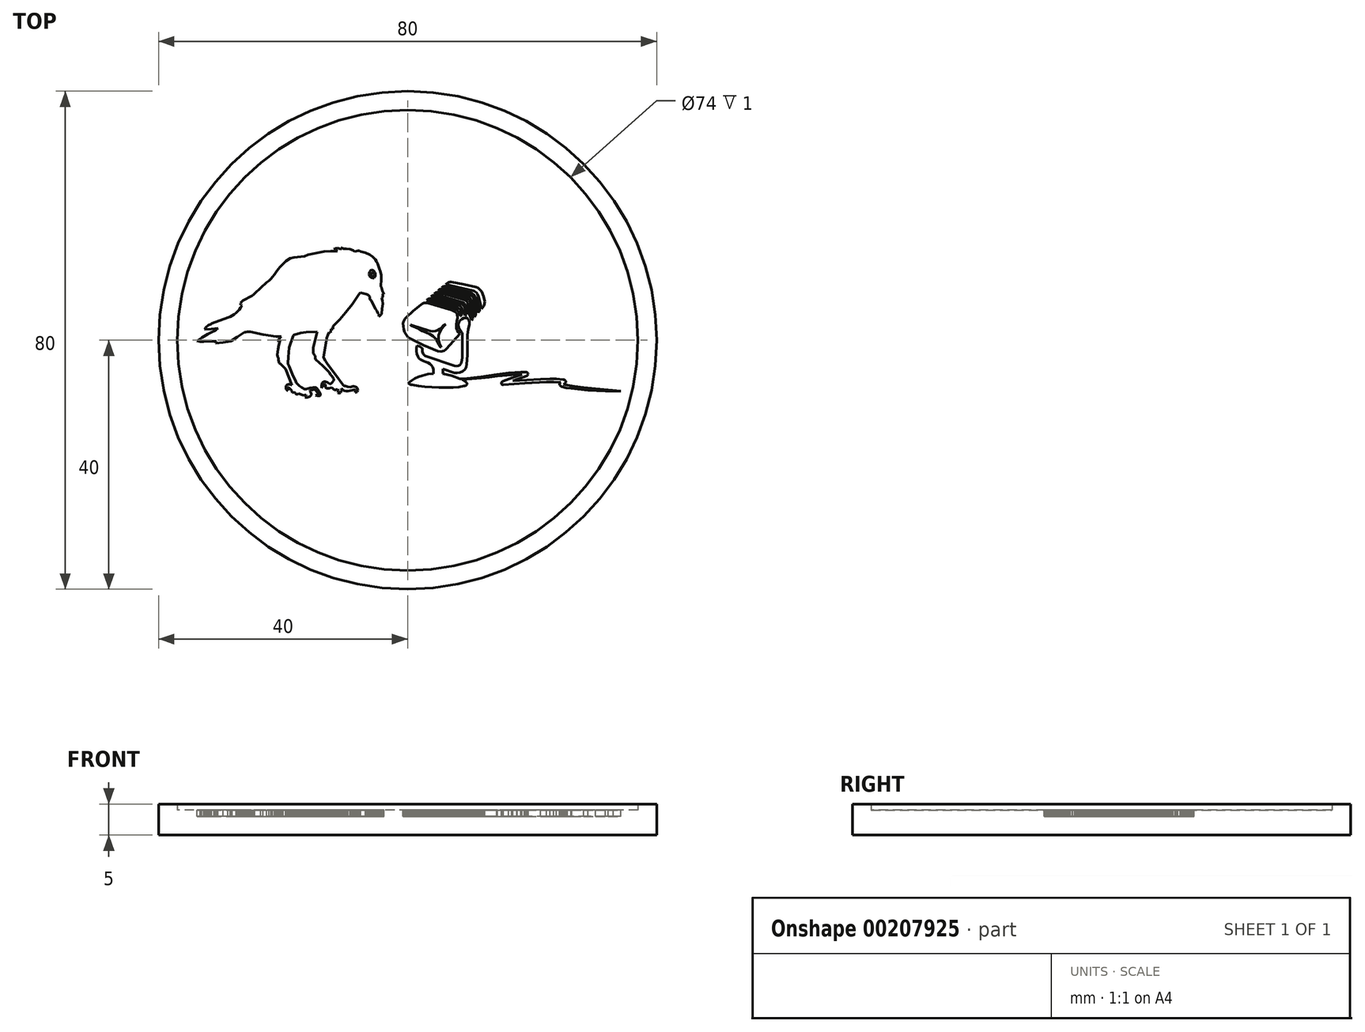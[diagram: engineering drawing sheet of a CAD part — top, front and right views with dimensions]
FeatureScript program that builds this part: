
annotation { "Feature Type Name" : "Feature", "Feature Type Description" : "" }
export const myFeature = defineFeature(function(context is Context, id is Id, definition is map)
    precondition{}
    {
        {
            var Q0;
            Q0=qCreatedBy(makeId("Top.planeOp"),FACE);
            var sketch = newSketch(context, id + "F0", { "sketchPlane" : qUnion([Q0])});
            skCircle(sketch, "E0", {"center": v(0, 0) * mm, "radius": 40 * mm});
            skSolve(sketch);
        }
        {
            var Q0;
            Q0 = qSketchRegion(id + "F0", true);
            extrude(context, id + "F1", {"entities" : qUnion([Q0]), "depth" : 4 * mm});
        }
        {
            var Q0;
            Q0=makeQuery(id+"F1.opExtrude","CAP_FACE",FACE,{"disambiguationData":[OSD([sQuery(id+"F0.wireOp",EDGE,"E0")])],"isStart":false});
            var sketch = newSketch(context, id + "F2", { "sketchPlane" : qUnion([Q0])});
            skCircle(sketch, "E1", {"center": v(0, 0) * mm, "radius": 37 * mm});
            skSolve(sketch);
        }
        {
            var Q0;
            Q0=makeQuery(id+"F2.imprint","IMPRINT",FACE,{"disambiguationData":[TD([[makeQuery(id+"F2.imprint","IMPRINT",EDGE,{"derivedFrom":sQuery(id+"F2.wireOp",EDGE,"E1")}),-1.0]])]});
            extrude(context, id + "F3", {"entities" : qUnion([Q0]), "operationType" : NewBodyOperationType.ADD, "depth" : 1 * mm});
        }
        {
            var Q0;
            Q0=makeQuery(id+"F3.opExtrude","CAP_FACE",FACE,{"disambiguationData":[OSD([sQuery(id+"F0.wireOp",EDGE,"E0"),sQuery(id+"F2.wireOp",EDGE,"E1")])],"isStart":false});
            var sketch = newSketch(context, id + "F4", { "sketchPlane" : qUnion([Q0])});
            skLineSegment(sketch, "E2", {"start": v(-11.88, 14.64) * mm, "end": v(-11.55, 14.76) * mm});
            skLineSegment(sketch, "E3", {"start": v(-11.55, 14.76) * mm, "end": v(-11.21, 14.85) * mm});
            skLineSegment(sketch, "E4", {"start": v(-11.21, 14.85) * mm, "end": v(-10.9, 14.72) * mm});
            skLineSegment(sketch, "E5", {"start": v(-10.9, 14.72) * mm, "end": v(-10.6, 14.6) * mm});
            skLineSegment(sketch, "E6", {"start": v(-10.6, 14.6) * mm, "end": v(-10.7, 14.86) * mm});
            skLineSegment(sketch, "E7", {"start": v(-10.7, 14.86) * mm, "end": v(-10.27, 14.72) * mm});
            skLineSegment(sketch, "E8", {"start": v(-10.27, 14.72) * mm, "end": v(-9.82, 14.67) * mm});
            skLineSegment(sketch, "E9", {"start": v(-9.82, 14.67) * mm, "end": v(-9.26, 14.64) * mm});
            skLineSegment(sketch, "E10", {"start": v(-9.26, 14.64) * mm, "end": v(-8.74, 14.43) * mm});
            skLineSegment(sketch, "E11", {"start": v(-8.74, 14.43) * mm, "end": v(-8.64, 14.34) * mm});
            skLineSegment(sketch, "E12", {"start": v(-8.64, 14.34) * mm, "end": v(-8.52, 14.28) * mm});
            skLineSegment(sketch, "E13", {"start": v(-8.52, 14.28) * mm, "end": v(-8.25, 14.33) * mm});
            skLineSegment(sketch, "E14", {"start": v(-8.25, 14.33) * mm, "end": v(-7.97, 14.38) * mm});
            skLineSegment(sketch, "E15", {"start": v(-7.97, 14.38) * mm, "end": v(-7.73, 14.35) * mm});
            skLineSegment(sketch, "E16", {"start": v(-7.73, 14.35) * mm, "end": v(-7.5, 14.28) * mm});
            skLineSegment(sketch, "E17", {"start": v(-7.5, 14.28) * mm, "end": v(-6.79, 14.04) * mm});
            skLineSegment(sketch, "E18", {"start": v(-6.79, 14.04) * mm, "end": v(-6.08, 13.75) * mm});
            skLineSegment(sketch, "E19", {"start": v(-6.08, 13.75) * mm, "end": v(-5.61, 13.4) * mm});
            skLineSegment(sketch, "E20", {"start": v(-5.61, 13.4) * mm, "end": v(-5.21, 12.98) * mm});
            skLineSegment(sketch, "E21", {"start": v(-5.21, 12.98) * mm, "end": v(-4.98, 12.64) * mm});
            skLineSegment(sketch, "E22", {"start": v(-4.98, 12.64) * mm, "end": v(-4.8, 12.27) * mm});
            skLineSegment(sketch, "E23", {"start": v(-4.8, 12.27) * mm, "end": v(-4.66, 11.89) * mm});
            skLineSegment(sketch, "E24", {"start": v(-4.66, 11.89) * mm, "end": v(-4.53, 11.5) * mm});
            skLineSegment(sketch, "E25", {"start": v(-4.53, 11.5) * mm, "end": v(-4.37, 10.99) * mm});
            skLineSegment(sketch, "E26", {"start": v(-4.37, 10.99) * mm, "end": v(-4.22, 10.47) * mm});
            skLineSegment(sketch, "E27", {"start": v(-4.22, 10.47) * mm, "end": v(-4.2, 9.64) * mm});
            skLineSegment(sketch, "E28", {"start": v(-4.2, 9.64) * mm, "end": v(-4.3, 8.82) * mm});
            skLineSegment(sketch, "E29", {"start": v(-4.3, 8.82) * mm, "end": v(-4.31, 8.71) * mm});
            skLineSegment(sketch, "E30", {"start": v(-4.31, 8.71) * mm, "end": v(-4.27, 8.6) * mm});
            skLineSegment(sketch, "E31", {"start": v(-4.27, 8.6) * mm, "end": v(-4.21, 8.51) * mm});
            skLineSegment(sketch, "E32", {"start": v(-4.21, 8.51) * mm, "end": v(-4.16, 8.41) * mm});
            skLineSegment(sketch, "E33", {"start": v(-4.16, 8.41) * mm, "end": v(-4.1, 8.15) * mm});
            skLineSegment(sketch, "E34", {"start": v(-4.1, 8.15) * mm, "end": v(-4.04, 7.88) * mm});
            skLineSegment(sketch, "E35", {"start": v(-4.04, 7.88) * mm, "end": v(-3.78, 7.4) * mm});
            skLineSegment(sketch, "E36", {"start": v(-3.78, 7.4) * mm, "end": v(-4, 7.46) * mm});
            skLineSegment(sketch, "E37", {"start": v(-4, 7.46) * mm, "end": v(-4, 6.95) * mm});
            skLineSegment(sketch, "E38", {"start": v(-4, 6.95) * mm, "end": v(-4.19, 6.85) * mm});
            skLineSegment(sketch, "E39", {"start": v(-4.19, 6.85) * mm, "end": v(-4.06, 6.36) * mm});
            skLineSegment(sketch, "E40", {"start": v(-4.06, 6.36) * mm, "end": v(-4, 5.85) * mm});
            skLineSegment(sketch, "E41", {"start": v(-4, 5.85) * mm, "end": v(-4.08, 5.07) * mm});
            skLineSegment(sketch, "E42", {"start": v(-4.08, 5.07) * mm, "end": v(-4.19, 4.3) * mm});
            skLineSegment(sketch, "E43", {"start": v(-4.19, 4.3) * mm, "end": v(-4.24, 4.14) * mm});
            skLineSegment(sketch, "E44", {"start": v(-4.24, 4.14) * mm, "end": v(-4.33, 4.02) * mm});
            skLineSegment(sketch, "E45", {"start": v(-4.33, 4.02) * mm, "end": v(-4.46, 3.92) * mm});
            skLineSegment(sketch, "E46", {"start": v(-4.46, 3.92) * mm, "end": v(-4.6, 3.83) * mm});
            skLineSegment(sketch, "E47", {"start": v(-4.6, 3.83) * mm, "end": v(-4.6, 4.02) * mm});
            skLineSegment(sketch, "E48", {"start": v(-4.6, 4.02) * mm, "end": v(-4.62, 4.2) * mm});
            skLineSegment(sketch, "E49", {"start": v(-4.62, 4.2) * mm, "end": v(-4.71, 4.3) * mm});
            skLineSegment(sketch, "E50", {"start": v(-4.71, 4.3) * mm, "end": v(-4.8, 4.39) * mm});
            skLineSegment(sketch, "E51", {"start": v(-4.8, 4.39) * mm, "end": v(-4.96, 4.7) * mm});
            skLineSegment(sketch, "E52", {"start": v(-4.96, 4.7) * mm, "end": v(-5.13, 4.99) * mm});
            skLineSegment(sketch, "E53", {"start": v(-5.13, 4.99) * mm, "end": v(-5.5, 5.68) * mm});
            skLineSegment(sketch, "E54", {"start": v(-5.5, 5.68) * mm, "end": v(-5.85, 6.38) * mm});
            skLineSegment(sketch, "E55", {"start": v(-5.85, 6.38) * mm, "end": v(-5.9, 6.44) * mm});
            skLineSegment(sketch, "E56", {"start": v(-5.9, 6.44) * mm, "end": v(-5.96, 6.48) * mm});
            skLineSegment(sketch, "E57", {"start": v(-5.96, 6.48) * mm, "end": v(-6.02, 6.52) * mm});
            skLineSegment(sketch, "E58", {"start": v(-6.02, 6.52) * mm, "end": v(-6.07, 6.58) * mm});
            skLineSegment(sketch, "E59", {"start": v(-6.07, 6.58) * mm, "end": v(-6.07, 7.02) * mm});
            skLineSegment(sketch, "E60", {"start": v(-6.07, 7.02) * mm, "end": v(-6.33, 7.23) * mm});
            skLineSegment(sketch, "E61", {"start": v(-6.33, 7.23) * mm, "end": v(-6.6, 7.42) * mm});
            skLineSegment(sketch, "E62", {"start": v(-6.6, 7.42) * mm, "end": v(-7.6, 7.64) * mm});
            skLineSegment(sketch, "E63", {"start": v(-7.6, 7.64) * mm, "end": v(-7.82, 7.35) * mm});
            skLineSegment(sketch, "E64", {"start": v(-7.82, 7.35) * mm, "end": v(-8.35, 6.6) * mm});
            skLineSegment(sketch, "E65", {"start": v(-8.35, 6.6) * mm, "end": v(-8.87, 5.83) * mm});
            skLineSegment(sketch, "E66", {"start": v(-8.87, 5.83) * mm, "end": v(-9.92, 4.46) * mm});
            skLineSegment(sketch, "E67", {"start": v(-9.92, 4.46) * mm, "end": v(-10.9, 3.32) * mm});
            skLineSegment(sketch, "E68", {"start": v(-10.9, 3.32) * mm, "end": v(-11.97, 2.24) * mm});
            skLineSegment(sketch, "E69", {"start": v(-11.97, 2.24) * mm, "end": v(-11.97, 1.82) * mm});
            skLineSegment(sketch, "E70", {"start": v(-11.97, 1.82) * mm, "end": v(-12.28, 1.82) * mm});
            skLineSegment(sketch, "E71", {"start": v(-12.28, 1.82) * mm, "end": v(-12.4, 1.22) * mm});
            skLineSegment(sketch, "E72", {"start": v(-12.4, 1.22) * mm, "end": v(-12.58, 1.32) * mm});
            skLineSegment(sketch, "E73", {"start": v(-12.58, 1.32) * mm, "end": v(-12.8, 0.82) * mm});
            skLineSegment(sketch, "E74", {"start": v(-12.8, 0.82) * mm, "end": v(-13.02, 0.32) * mm});
            skLineSegment(sketch, "E75", {"start": v(-13.02, 0.32) * mm, "end": v(-13.53, -2.78) * mm});
            skLineSegment(sketch, "E76", {"start": v(-13.53, -2.78) * mm, "end": v(-13.17, -3.35) * mm});
            skLineSegment(sketch, "E77", {"start": v(-13.17, -3.35) * mm, "end": v(-12.78, -3.9) * mm});
            skLineSegment(sketch, "E78", {"start": v(-12.78, -3.9) * mm, "end": v(-11.6, -5.52) * mm});
            skLineSegment(sketch, "E79", {"start": v(-11.6, -5.52) * mm, "end": v(-10.42, -7.13) * mm});
            skLineSegment(sketch, "E80", {"start": v(-10.42, -7.13) * mm, "end": v(-10.34, -7.21) * mm});
            skLineSegment(sketch, "E81", {"start": v(-10.34, -7.21) * mm, "end": v(-10.24, -7.27) * mm});
            skLineSegment(sketch, "E82", {"start": v(-10.24, -7.27) * mm, "end": v(-10.13, -7.32) * mm});
            skLineSegment(sketch, "E83", {"start": v(-10.13, -7.32) * mm, "end": v(-10.03, -7.36) * mm});
            skLineSegment(sketch, "E84", {"start": v(-10.03, -7.36) * mm, "end": v(-9.62, -7.5) * mm});
            skLineSegment(sketch, "E85", {"start": v(-9.62, -7.5) * mm, "end": v(-9.2, -7.53) * mm});
            skLineSegment(sketch, "E86", {"start": v(-9.2, -7.53) * mm, "end": v(-9.01, -7.48) * mm});
            skLineSegment(sketch, "E87", {"start": v(-9.01, -7.48) * mm, "end": v(-8.82, -7.43) * mm});
            skLineSegment(sketch, "E88", {"start": v(-8.82, -7.43) * mm, "end": v(-8.63, -7.42) * mm});
            skLineSegment(sketch, "E89", {"start": v(-8.63, -7.42) * mm, "end": v(-8.43, -7.46) * mm});
            skLineSegment(sketch, "E90", {"start": v(-8.43, -7.46) * mm, "end": v(-8.25, -7.53) * mm});
            skLineSegment(sketch, "E91", {"start": v(-8.25, -7.53) * mm, "end": v(-8.12, -7.66) * mm});
            skLineSegment(sketch, "E92", {"start": v(-8.12, -7.66) * mm, "end": v(-8.04, -7.84) * mm});
            skLineSegment(sketch, "E93", {"start": v(-8.04, -7.84) * mm, "end": v(-8, -8.02) * mm});
            skLineSegment(sketch, "E94", {"start": v(-8, -8.02) * mm, "end": v(-8.04, -8.17) * mm});
            skLineSegment(sketch, "E95", {"start": v(-8.04, -8.17) * mm, "end": v(-8.1, -8.32) * mm});
            skLineSegment(sketch, "E96", {"start": v(-8.1, -8.32) * mm, "end": v(-8.42, -8.41) * mm});
            skLineSegment(sketch, "E97", {"start": v(-8.42, -8.41) * mm, "end": v(-8.37, -8.22) * mm});
            skLineSegment(sketch, "E98", {"start": v(-8.37, -8.22) * mm, "end": v(-8.37, -8.03) * mm});
            skLineSegment(sketch, "E99", {"start": v(-8.37, -8.03) * mm, "end": v(-8.5, -7.97) * mm});
            skLineSegment(sketch, "E100", {"start": v(-8.5, -7.97) * mm, "end": v(-8.63, -7.96) * mm});
            skLineSegment(sketch, "E101", {"start": v(-8.63, -7.96) * mm, "end": v(-8.77, -7.99) * mm});
            skLineSegment(sketch, "E102", {"start": v(-8.77, -7.99) * mm, "end": v(-8.9, -8.02) * mm});
            skLineSegment(sketch, "E103", {"start": v(-8.9, -8.02) * mm, "end": v(-9.23, -8.1) * mm});
            skLineSegment(sketch, "E104", {"start": v(-9.23, -8.1) * mm, "end": v(-9.55, -8.16) * mm});
            skLineSegment(sketch, "E105", {"start": v(-9.55, -8.16) * mm, "end": v(-9.88, -8.18) * mm});
            skLineSegment(sketch, "E106", {"start": v(-9.88, -8.18) * mm, "end": v(-10.2, -8.1) * mm});
            skLineSegment(sketch, "E107", {"start": v(-10.2, -8.1) * mm, "end": v(-10.43, -7.92) * mm});
            skLineSegment(sketch, "E108", {"start": v(-10.43, -7.92) * mm, "end": v(-10.65, -7.74) * mm});
            skLineSegment(sketch, "E109", {"start": v(-10.65, -7.74) * mm, "end": v(-10.61, -7.88) * mm});
            skLineSegment(sketch, "E110", {"start": v(-10.61, -7.88) * mm, "end": v(-10.6, -8.03) * mm});
            skLineSegment(sketch, "E111", {"start": v(-10.6, -8.03) * mm, "end": v(-10.61, -8.17) * mm});
            skLineSegment(sketch, "E112", {"start": v(-10.61, -8.17) * mm, "end": v(-10.68, -8.3) * mm});
            skLineSegment(sketch, "E113", {"start": v(-10.68, -8.3) * mm, "end": v(-10.79, -8.42) * mm});
            skLineSegment(sketch, "E114", {"start": v(-10.79, -8.42) * mm, "end": v(-10.92, -8.48) * mm});
            skLineSegment(sketch, "E115", {"start": v(-10.92, -8.48) * mm, "end": v(-11.08, -8.5) * mm});
            skLineSegment(sketch, "E116", {"start": v(-11.08, -8.5) * mm, "end": v(-11.24, -8.45) * mm});
            skLineSegment(sketch, "E117", {"start": v(-11.24, -8.45) * mm, "end": v(-11.16, -8.29) * mm});
            skLineSegment(sketch, "E118", {"start": v(-11.16, -8.29) * mm, "end": v(-11.1, -8.12) * mm});
            skLineSegment(sketch, "E119", {"start": v(-11.1, -8.12) * mm, "end": v(-11.13, -7.98) * mm});
            skLineSegment(sketch, "E120", {"start": v(-11.13, -7.98) * mm, "end": v(-11.2, -7.84) * mm});
            skLineSegment(sketch, "E121", {"start": v(-11.2, -7.84) * mm, "end": v(-11.3, -7.89) * mm});
            skLineSegment(sketch, "E122", {"start": v(-11.3, -7.89) * mm, "end": v(-11.4, -7.94) * mm});
            skLineSegment(sketch, "E123", {"start": v(-11.4, -7.94) * mm, "end": v(-11.5, -7.98) * mm});
            skLineSegment(sketch, "E124", {"start": v(-11.5, -7.98) * mm, "end": v(-11.62, -7.99) * mm});
            skLineSegment(sketch, "E125", {"start": v(-11.62, -7.99) * mm, "end": v(-11.8, -7.96) * mm});
            skLineSegment(sketch, "E126", {"start": v(-11.8, -7.96) * mm, "end": v(-11.94, -7.87) * mm});
            skLineSegment(sketch, "E127", {"start": v(-11.94, -7.87) * mm, "end": v(-12.07, -7.75) * mm});
            skLineSegment(sketch, "E128", {"start": v(-12.07, -7.75) * mm, "end": v(-12.19, -7.61) * mm});
            skLineSegment(sketch, "E129", {"start": v(-12.19, -7.61) * mm, "end": v(-12.6, -7.72) * mm});
            skLineSegment(sketch, "E130", {"start": v(-12.6, -7.72) * mm, "end": v(-13.04, -7.7) * mm});
            skLineSegment(sketch, "E131", {"start": v(-13.04, -7.7) * mm, "end": v(-13.17, -7.6) * mm});
            skLineSegment(sketch, "E132", {"start": v(-13.17, -7.6) * mm, "end": v(-13.2, -7.44) * mm});
            skLineSegment(sketch, "E133", {"start": v(-13.2, -7.44) * mm, "end": v(-13.2, -7.26) * mm});
            skLineSegment(sketch, "E134", {"start": v(-13.2, -7.26) * mm, "end": v(-13.16, -7.1) * mm});
            skLineSegment(sketch, "E135", {"start": v(-13.16, -7.1) * mm, "end": v(-13.24, -7.1) * mm});
            skLineSegment(sketch, "E136", {"start": v(-13.24, -7.1) * mm, "end": v(-13.32, -7.1) * mm});
            skLineSegment(sketch, "E137", {"start": v(-13.32, -7.1) * mm, "end": v(-13.4, -7.12) * mm});
            skLineSegment(sketch, "E138", {"start": v(-13.4, -7.12) * mm, "end": v(-13.45, -7.17) * mm});
            skLineSegment(sketch, "E139", {"start": v(-13.45, -7.17) * mm, "end": v(-13.63, -7.43) * mm});
            skLineSegment(sketch, "E140", {"start": v(-13.63, -7.43) * mm, "end": v(-13.82, -7.67) * mm});
            skLineSegment(sketch, "E141", {"start": v(-13.82, -7.67) * mm, "end": v(-13.8, -7.26) * mm});
            skLineSegment(sketch, "E142", {"start": v(-13.8, -7.26) * mm, "end": v(-13.7, -6.86) * mm});
            skLineSegment(sketch, "E143", {"start": v(-13.7, -6.86) * mm, "end": v(-13.63, -6.75) * mm});
            skLineSegment(sketch, "E144", {"start": v(-13.63, -6.75) * mm, "end": v(-13.52, -6.68) * mm});
            skLineSegment(sketch, "E145", {"start": v(-13.52, -6.68) * mm, "end": v(-13.4, -6.65) * mm});
            skLineSegment(sketch, "E146", {"start": v(-13.4, -6.65) * mm, "end": v(-13.27, -6.64) * mm});
            skLineSegment(sketch, "E147", {"start": v(-13.27, -6.64) * mm, "end": v(-13.05, -6.68) * mm});
            skLineSegment(sketch, "E148", {"start": v(-13.05, -6.68) * mm, "end": v(-12.84, -6.76) * mm});
            skLineSegment(sketch, "E149", {"start": v(-12.84, -6.76) * mm, "end": v(-12.65, -6.87) * mm});
            skLineSegment(sketch, "E150", {"start": v(-12.65, -6.87) * mm, "end": v(-12.48, -7.01) * mm});
            skLineSegment(sketch, "E151", {"start": v(-12.48, -7.01) * mm, "end": v(-12.4, -7.02) * mm});
            skLineSegment(sketch, "E152", {"start": v(-12.4, -7.02) * mm, "end": v(-12.13, -6.78) * mm});
            skLineSegment(sketch, "E153", {"start": v(-12.13, -6.78) * mm, "end": v(-11.9, -6.51) * mm});
            skLineSegment(sketch, "E154", {"start": v(-11.9, -6.51) * mm, "end": v(-11.83, -6.36) * mm});
            skLineSegment(sketch, "E155", {"start": v(-11.83, -6.36) * mm, "end": v(-11.88, -6.2) * mm});
            skLineSegment(sketch, "E156", {"start": v(-11.88, -6.2) * mm, "end": v(-11.97, -6.05) * mm});
            skLineSegment(sketch, "E157", {"start": v(-11.97, -6.05) * mm, "end": v(-12.07, -5.91) * mm});
            skLineSegment(sketch, "E158", {"start": v(-12.07, -5.91) * mm, "end": v(-12.35, -5.54) * mm});
            skLineSegment(sketch, "E159", {"start": v(-12.35, -5.54) * mm, "end": v(-12.6, -5.15) * mm});
            skLineSegment(sketch, "E160", {"start": v(-12.6, -5.15) * mm, "end": v(-13.65, -4.07) * mm});
            skLineSegment(sketch, "E161", {"start": v(-13.65, -4.07) * mm, "end": v(-14.77, -3.06) * mm});
            skLineSegment(sketch, "E162", {"start": v(-14.77, -3.06) * mm, "end": v(-14.82, -2.9) * mm});
            skLineSegment(sketch, "E163", {"start": v(-14.82, -2.9) * mm, "end": v(-14.83, -2.74) * mm});
            skLineSegment(sketch, "E164", {"start": v(-14.83, -2.74) * mm, "end": v(-14.85, -2.58) * mm});
            skLineSegment(sketch, "E165", {"start": v(-14.85, -2.58) * mm, "end": v(-14.92, -2.44) * mm});
            skLineSegment(sketch, "E166", {"start": v(-14.92, -2.44) * mm, "end": v(-15.05, -2.28) * mm});
            skLineSegment(sketch, "E167", {"start": v(-15.05, -2.28) * mm, "end": v(-15.16, -2.1) * mm});
            skLineSegment(sketch, "E168", {"start": v(-15.16, -2.1) * mm, "end": v(-15.15, -1.2) * mm});
            skLineSegment(sketch, "E169", {"start": v(-15.15, -1.2) * mm, "end": v(-14.53, 1.39) * mm});
            skLineSegment(sketch, "E170", {"start": v(-14.53, 1.39) * mm, "end": v(-16.3, 1.28) * mm});
            skLineSegment(sketch, "E171", {"start": v(-16.3, 1.28) * mm, "end": v(-16.73, 1.25) * mm});
            skLineSegment(sketch, "E172", {"start": v(-16.73, 1.25) * mm, "end": v(-17.16, 1.17) * mm});
            skLineSegment(sketch, "E173", {"start": v(-17.16, 1.17) * mm, "end": v(-18.27, 0.84) * mm});
            skLineSegment(sketch, "E174", {"start": v(-18.27, 0.84) * mm, "end": v(-18.34, 0.77) * mm});
            skLineSegment(sketch, "E175", {"start": v(-18.34, 0.77) * mm, "end": v(-18.37, 0.68) * mm});
            skLineSegment(sketch, "E176", {"start": v(-18.37, 0.68) * mm, "end": v(-19.05, -1.2) * mm});
            skLineSegment(sketch, "E177", {"start": v(-19.05, -1.2) * mm, "end": v(-19.11, -1.94) * mm});
            skLineSegment(sketch, "E178", {"start": v(-19.11, -1.94) * mm, "end": v(-19.15, -2.68) * mm});
            skLineSegment(sketch, "E179", {"start": v(-19.15, -2.68) * mm, "end": v(-19.2, -3.66) * mm});
            skLineSegment(sketch, "E180", {"start": v(-19.2, -3.66) * mm, "end": v(-19.2, -3.8) * mm});
            skLineSegment(sketch, "E181", {"start": v(-19.2, -3.8) * mm, "end": v(-19.16, -3.92) * mm});
            skLineSegment(sketch, "E182", {"start": v(-19.16, -3.92) * mm, "end": v(-19.1, -4.04) * mm});
            skLineSegment(sketch, "E183", {"start": v(-19.1, -4.04) * mm, "end": v(-19.06, -4.16) * mm});
            skLineSegment(sketch, "E184", {"start": v(-19.06, -4.16) * mm, "end": v(-18.52, -5.42) * mm});
            skLineSegment(sketch, "E185", {"start": v(-18.52, -5.42) * mm, "end": v(-17.97, -6.67) * mm});
            skLineSegment(sketch, "E186", {"start": v(-17.97, -6.67) * mm, "end": v(-17.86, -6.86) * mm});
            skLineSegment(sketch, "E187", {"start": v(-17.86, -6.86) * mm, "end": v(-17.72, -7.03) * mm});
            skLineSegment(sketch, "E188", {"start": v(-17.72, -7.03) * mm, "end": v(-17.55, -7.18) * mm});
            skLineSegment(sketch, "E189", {"start": v(-17.55, -7.18) * mm, "end": v(-17.38, -7.32) * mm});
            skLineSegment(sketch, "E190", {"start": v(-17.38, -7.32) * mm, "end": v(-16.98, -7.61) * mm});
            skLineSegment(sketch, "E191", {"start": v(-16.98, -7.61) * mm, "end": v(-16.54, -7.86) * mm});
            skLineSegment(sketch, "E192", {"start": v(-16.54, -7.86) * mm, "end": v(-16.31, -7.87) * mm});
            skLineSegment(sketch, "E193", {"start": v(-16.31, -7.87) * mm, "end": v(-16.1, -7.81) * mm});
            skLineSegment(sketch, "E194", {"start": v(-16.1, -7.81) * mm, "end": v(-15.88, -7.74) * mm});
            skLineSegment(sketch, "E195", {"start": v(-15.88, -7.74) * mm, "end": v(-15.66, -7.68) * mm});
            skLineSegment(sketch, "E196", {"start": v(-15.66, -7.68) * mm, "end": v(-15.23, -7.62) * mm});
            skLineSegment(sketch, "E197", {"start": v(-15.23, -7.62) * mm, "end": v(-14.8, -7.61) * mm});
            skLineSegment(sketch, "E198", {"start": v(-14.8, -7.61) * mm, "end": v(-14.65, -7.68) * mm});
            skLineSegment(sketch, "E199", {"start": v(-14.65, -7.68) * mm, "end": v(-14.52, -7.8) * mm});
            skLineSegment(sketch, "E200", {"start": v(-14.52, -7.8) * mm, "end": v(-14.21, -8.2) * mm});
            skLineSegment(sketch, "E201", {"start": v(-14.21, -8.2) * mm, "end": v(-14, -8.68) * mm});
            skLineSegment(sketch, "E202", {"start": v(-14, -8.68) * mm, "end": v(-14, -8.76) * mm});
            skLineSegment(sketch, "E203", {"start": v(-14, -8.76) * mm, "end": v(-14.02, -8.84) * mm});
            skLineSegment(sketch, "E204", {"start": v(-14.02, -8.84) * mm, "end": v(-14.07, -8.9) * mm});
            skLineSegment(sketch, "E205", {"start": v(-14.07, -8.9) * mm, "end": v(-14.15, -8.94) * mm});
            skLineSegment(sketch, "E206", {"start": v(-14.15, -8.94) * mm, "end": v(-14.46, -8.95) * mm});
            skLineSegment(sketch, "E207", {"start": v(-14.46, -8.95) * mm, "end": v(-14.77, -8.88) * mm});
            skLineSegment(sketch, "E208", {"start": v(-14.77, -8.88) * mm, "end": v(-14.66, -8.83) * mm});
            skLineSegment(sketch, "E209", {"start": v(-14.66, -8.83) * mm, "end": v(-14.54, -8.78) * mm});
            skLineSegment(sketch, "E210", {"start": v(-14.54, -8.78) * mm, "end": v(-14.44, -8.73) * mm});
            skLineSegment(sketch, "E211", {"start": v(-14.44, -8.73) * mm, "end": v(-14.36, -8.64) * mm});
            skLineSegment(sketch, "E212", {"start": v(-14.36, -8.64) * mm, "end": v(-14.43, -8.44) * mm});
            skLineSegment(sketch, "E213", {"start": v(-14.43, -8.44) * mm, "end": v(-14.56, -8.28) * mm});
            skLineSegment(sketch, "E214", {"start": v(-14.56, -8.28) * mm, "end": v(-14.72, -8.13) * mm});
            skLineSegment(sketch, "E215", {"start": v(-14.72, -8.13) * mm, "end": v(-14.87, -8) * mm});
            skLineSegment(sketch, "E216", {"start": v(-14.87, -8) * mm, "end": v(-14.95, -7.94) * mm});
            skLineSegment(sketch, "E217", {"start": v(-14.95, -7.94) * mm, "end": v(-15.04, -7.93) * mm});
            skLineSegment(sketch, "E218", {"start": v(-15.04, -7.93) * mm, "end": v(-15.13, -7.94) * mm});
            skLineSegment(sketch, "E219", {"start": v(-15.13, -7.94) * mm, "end": v(-15.23, -7.95) * mm});
            skLineSegment(sketch, "E220", {"start": v(-15.23, -7.95) * mm, "end": v(-15.37, -7.96) * mm});
            skLineSegment(sketch, "E221", {"start": v(-15.37, -7.96) * mm, "end": v(-15.52, -8) * mm});
            skLineSegment(sketch, "E222", {"start": v(-15.52, -8) * mm, "end": v(-15.65, -8.06) * mm});
            skLineSegment(sketch, "E223", {"start": v(-15.65, -8.06) * mm, "end": v(-15.75, -8.17) * mm});
            skLineSegment(sketch, "E224", {"start": v(-15.75, -8.17) * mm, "end": v(-15.63, -8.3) * mm});
            skLineSegment(sketch, "E225", {"start": v(-15.63, -8.3) * mm, "end": v(-15.53, -8.44) * mm});
            skLineSegment(sketch, "E226", {"start": v(-15.53, -8.44) * mm, "end": v(-15.48, -8.6) * mm});
            skLineSegment(sketch, "E227", {"start": v(-15.48, -8.6) * mm, "end": v(-15.5, -8.77) * mm});
            skLineSegment(sketch, "E228", {"start": v(-15.5, -8.77) * mm, "end": v(-15.53, -8.86) * mm});
            skLineSegment(sketch, "E229", {"start": v(-15.53, -8.86) * mm, "end": v(-15.59, -8.93) * mm});
            skLineSegment(sketch, "E230", {"start": v(-15.59, -8.93) * mm, "end": v(-15.66, -8.99) * mm});
            skLineSegment(sketch, "E231", {"start": v(-15.66, -8.99) * mm, "end": v(-15.75, -9.04) * mm});
            skLineSegment(sketch, "E232", {"start": v(-15.75, -9.04) * mm, "end": v(-15.91, -9.11) * mm});
            skLineSegment(sketch, "E233", {"start": v(-15.91, -9.11) * mm, "end": v(-16.1, -9.15) * mm});
            skLineSegment(sketch, "E234", {"start": v(-16.1, -9.15) * mm, "end": v(-16.28, -9.18) * mm});
            skLineSegment(sketch, "E235", {"start": v(-16.28, -9.18) * mm, "end": v(-16.46, -9.2) * mm});
            skLineSegment(sketch, "E236", {"start": v(-16.46, -9.2) * mm, "end": v(-16.38, -9.11) * mm});
            skLineSegment(sketch, "E237", {"start": v(-16.38, -9.11) * mm, "end": v(-16.3, -9.02) * mm});
            skLineSegment(sketch, "E238", {"start": v(-16.3, -9.02) * mm, "end": v(-16.26, -8.9) * mm});
            skLineSegment(sketch, "E239", {"start": v(-16.26, -8.9) * mm, "end": v(-16.29, -8.78) * mm});
            skLineSegment(sketch, "E240", {"start": v(-16.29, -8.78) * mm, "end": v(-16.48, -8.82) * mm});
            skLineSegment(sketch, "E241", {"start": v(-16.48, -8.82) * mm, "end": v(-16.66, -8.9) * mm});
            skLineSegment(sketch, "E242", {"start": v(-16.66, -8.9) * mm, "end": v(-17.08, -8.76) * mm});
            skLineSegment(sketch, "E243", {"start": v(-17.08, -8.76) * mm, "end": v(-17.48, -8.57) * mm});
            skLineSegment(sketch, "E244", {"start": v(-17.48, -8.57) * mm, "end": v(-17.56, -8.61) * mm});
            skLineSegment(sketch, "E245", {"start": v(-17.56, -8.61) * mm, "end": v(-17.64, -8.65) * mm});
            skLineSegment(sketch, "E246", {"start": v(-17.64, -8.65) * mm, "end": v(-17.73, -8.68) * mm});
            skLineSegment(sketch, "E247", {"start": v(-17.73, -8.68) * mm, "end": v(-17.82, -8.68) * mm});
            skLineSegment(sketch, "E248", {"start": v(-17.82, -8.68) * mm, "end": v(-17.93, -8.62) * mm});
            skLineSegment(sketch, "E249", {"start": v(-17.93, -8.62) * mm, "end": v(-18.02, -8.53) * mm});
            skLineSegment(sketch, "E250", {"start": v(-18.02, -8.53) * mm, "end": v(-18.1, -8.43) * mm});
            skLineSegment(sketch, "E251", {"start": v(-18.1, -8.43) * mm, "end": v(-18.17, -8.33) * mm});
            skLineSegment(sketch, "E252", {"start": v(-18.17, -8.33) * mm, "end": v(-18.5, -8.4) * mm});
            skLineSegment(sketch, "E253", {"start": v(-18.5, -8.4) * mm, "end": v(-18.61, -8.19) * mm});
            skLineSegment(sketch, "E254", {"start": v(-18.61, -8.19) * mm, "end": v(-18.73, -7.99) * mm});
            skLineSegment(sketch, "E255", {"start": v(-18.73, -7.99) * mm, "end": v(-18.87, -7.8) * mm});
            skLineSegment(sketch, "E256", {"start": v(-18.87, -7.8) * mm, "end": v(-19.03, -7.63) * mm});
            skLineSegment(sketch, "E257", {"start": v(-19.03, -7.63) * mm, "end": v(-19.09, -7.59) * mm});
            skLineSegment(sketch, "E258", {"start": v(-19.09, -7.59) * mm, "end": v(-19.16, -7.56) * mm});
            skLineSegment(sketch, "E259", {"start": v(-19.16, -7.56) * mm, "end": v(-19.22, -7.57) * mm});
            skLineSegment(sketch, "E260", {"start": v(-19.22, -7.57) * mm, "end": v(-19.27, -7.63) * mm});
            skLineSegment(sketch, "E261", {"start": v(-19.27, -7.63) * mm, "end": v(-19.27, -7.86) * mm});
            skLineSegment(sketch, "E262", {"start": v(-19.27, -7.86) * mm, "end": v(-19.22, -8.09) * mm});
            skLineSegment(sketch, "E263", {"start": v(-19.22, -8.09) * mm, "end": v(-19.35, -8) * mm});
            skLineSegment(sketch, "E264", {"start": v(-19.35, -8) * mm, "end": v(-19.46, -7.9) * mm});
            skLineSegment(sketch, "E265", {"start": v(-19.46, -7.9) * mm, "end": v(-19.53, -7.77) * mm});
            skLineSegment(sketch, "E266", {"start": v(-19.53, -7.77) * mm, "end": v(-19.54, -7.61) * mm});
            skLineSegment(sketch, "E267", {"start": v(-19.54, -7.61) * mm, "end": v(-19.53, -7.44) * mm});
            skLineSegment(sketch, "E268", {"start": v(-19.53, -7.44) * mm, "end": v(-19.45, -7.28) * mm});
            skLineSegment(sketch, "E269", {"start": v(-19.45, -7.28) * mm, "end": v(-19.33, -7.16) * mm});
            skLineSegment(sketch, "E270", {"start": v(-19.33, -7.16) * mm, "end": v(-19.17, -7.08) * mm});
            skLineSegment(sketch, "E271", {"start": v(-19.17, -7.08) * mm, "end": v(-18.88, -7.1) * mm});
            skLineSegment(sketch, "E272", {"start": v(-18.88, -7.1) * mm, "end": v(-18.6, -7.18) * mm});
            skLineSegment(sketch, "E273", {"start": v(-18.6, -7.18) * mm, "end": v(-19.61, -4.61) * mm});
            skLineSegment(sketch, "E274", {"start": v(-19.61, -4.61) * mm, "end": v(-19.97, -4.23) * mm});
            skLineSegment(sketch, "E275", {"start": v(-19.97, -4.23) * mm, "end": v(-20.36, -3.87) * mm});
            skLineSegment(sketch, "E276", {"start": v(-20.36, -3.87) * mm, "end": v(-20.45, -3.8) * mm});
            skLineSegment(sketch, "E277", {"start": v(-20.45, -3.8) * mm, "end": v(-20.54, -3.73) * mm});
            skLineSegment(sketch, "E278", {"start": v(-20.54, -3.73) * mm, "end": v(-20.62, -3.65) * mm});
            skLineSegment(sketch, "E279", {"start": v(-20.62, -3.65) * mm, "end": v(-20.66, -3.55) * mm});
            skLineSegment(sketch, "E280", {"start": v(-20.66, -3.55) * mm, "end": v(-20.7, -3.4) * mm});
            skLineSegment(sketch, "E281", {"start": v(-20.7, -3.4) * mm, "end": v(-20.72, -3.24) * mm});
            skLineSegment(sketch, "E282", {"start": v(-20.72, -3.24) * mm, "end": v(-20.73, -3.08) * mm});
            skLineSegment(sketch, "E283", {"start": v(-20.73, -3.08) * mm, "end": v(-20.76, -2.92) * mm});
            skLineSegment(sketch, "E284", {"start": v(-20.76, -2.92) * mm, "end": v(-20.87, -2.63) * mm});
            skLineSegment(sketch, "E285", {"start": v(-20.87, -2.63) * mm, "end": v(-20.91, -2.33) * mm});
            skLineSegment(sketch, "E286", {"start": v(-20.91, -2.33) * mm, "end": v(-20.8, -1.41) * mm});
            skLineSegment(sketch, "E287", {"start": v(-20.8, -1.41) * mm, "end": v(-20.68, -0.73) * mm});
            skLineSegment(sketch, "E288", {"start": v(-20.68, -0.73) * mm, "end": v(-20.51, -0.05) * mm});
            skLineSegment(sketch, "E289", {"start": v(-20.51, -0.05) * mm, "end": v(-20.96, -0.13) * mm});
            skLineSegment(sketch, "E290", {"start": v(-20.96, -0.13) * mm, "end": v(-20.63, 0.23) * mm});
            skLineSegment(sketch, "E291", {"start": v(-20.63, 0.23) * mm, "end": v(-20.3, 0.6) * mm});
            skLineSegment(sketch, "E292", {"start": v(-20.3, 0.6) * mm, "end": v(-20.7, 0.6) * mm});
            skLineSegment(sketch, "E293", {"start": v(-20.7, 0.6) * mm, "end": v(-21.1, 0.62) * mm});
            skLineSegment(sketch, "E294", {"start": v(-21.1, 0.62) * mm, "end": v(-23.2, 0.94) * mm});
            skLineSegment(sketch, "E295", {"start": v(-23.2, 0.94) * mm, "end": v(-25.26, 1.35) * mm});
            skLineSegment(sketch, "E296", {"start": v(-25.26, 1.35) * mm, "end": v(-25.5, 1.35) * mm});
            skLineSegment(sketch, "E297", {"start": v(-25.5, 1.35) * mm, "end": v(-25.75, 1.33) * mm});
            skLineSegment(sketch, "E298", {"start": v(-25.75, 1.33) * mm, "end": v(-25.99, 1.32) * mm});
            skLineSegment(sketch, "E299", {"start": v(-25.99, 1.32) * mm, "end": v(-26.22, 1.28) * mm});
            skLineSegment(sketch, "E300", {"start": v(-26.22, 1.28) * mm, "end": v(-27.33, 0.56) * mm});
            skLineSegment(sketch, "E301", {"start": v(-27.33, 0.56) * mm, "end": v(-28.44, -0.14) * mm});
            skLineSegment(sketch, "E302", {"start": v(-28.44, -0.14) * mm, "end": v(-29.62, -0.35) * mm});
            skLineSegment(sketch, "E303", {"start": v(-29.62, -0.35) * mm, "end": v(-30.81, -0.47) * mm});
            skLineSegment(sketch, "E304", {"start": v(-30.81, -0.47) * mm, "end": v(-30.69, -0.14) * mm});
            skLineSegment(sketch, "E305", {"start": v(-30.69, -0.14) * mm, "end": v(-31.72, -0.16) * mm});
            skLineSegment(sketch, "E306", {"start": v(-31.72, -0.16) * mm, "end": v(-32.74, -0.23) * mm});
            skLineSegment(sketch, "E307", {"start": v(-32.74, -0.23) * mm, "end": v(-33.3, -0.24) * mm});
            skLineSegment(sketch, "E308", {"start": v(-33.3, -0.24) * mm, "end": v(-33.84, -0.11) * mm});
            skLineSegment(sketch, "E309", {"start": v(-33.84, -0.11) * mm, "end": v(-33.07, 0.43) * mm});
            skLineSegment(sketch, "E310", {"start": v(-33.07, 0.43) * mm, "end": v(-32.08, 0.96) * mm});
            skLineSegment(sketch, "E311", {"start": v(-32.08, 0.96) * mm, "end": v(-31.08, 1.47) * mm});
            skLineSegment(sketch, "E312", {"start": v(-31.08, 1.47) * mm, "end": v(-30.75, 1.68) * mm});
            skLineSegment(sketch, "E313", {"start": v(-30.75, 1.68) * mm, "end": v(-30.45, 1.93) * mm});
            skLineSegment(sketch, "E314", {"start": v(-30.45, 1.93) * mm, "end": v(-31.52, 1.82) * mm});
            skLineSegment(sketch, "E315", {"start": v(-31.52, 1.82) * mm, "end": v(-32.6, 1.77) * mm});
            skLineSegment(sketch, "E316", {"start": v(-32.6, 1.77) * mm, "end": v(-32.51, 1.93) * mm});
            skLineSegment(sketch, "E317", {"start": v(-32.51, 1.93) * mm, "end": v(-32.4, 2.07) * mm});
            skLineSegment(sketch, "E318", {"start": v(-32.4, 2.07) * mm, "end": v(-32.27, 2.2) * mm});
            skLineSegment(sketch, "E319", {"start": v(-32.27, 2.2) * mm, "end": v(-32.14, 2.32) * mm});
            skLineSegment(sketch, "E320", {"start": v(-32.14, 2.32) * mm, "end": v(-31.98, 2.43) * mm});
            skLineSegment(sketch, "E321", {"start": v(-31.98, 2.43) * mm, "end": v(-31.8, 2.52) * mm});
            skLineSegment(sketch, "E322", {"start": v(-31.8, 2.52) * mm, "end": v(-31.63, 2.6) * mm});
            skLineSegment(sketch, "E323", {"start": v(-31.63, 2.6) * mm, "end": v(-31.45, 2.66) * mm});
            skLineSegment(sketch, "E324", {"start": v(-31.45, 2.66) * mm, "end": v(-28.86, 3.62) * mm});
            skLineSegment(sketch, "E325", {"start": v(-28.86, 3.62) * mm, "end": v(-28.5, 3.76) * mm});
            skLineSegment(sketch, "E326", {"start": v(-28.5, 3.76) * mm, "end": v(-28.17, 3.96) * mm});
            skLineSegment(sketch, "E327", {"start": v(-28.17, 3.96) * mm, "end": v(-27.84, 4.17) * mm});
            skLineSegment(sketch, "E328", {"start": v(-27.84, 4.17) * mm, "end": v(-27.52, 4.4) * mm});
            skLineSegment(sketch, "E329", {"start": v(-27.52, 4.4) * mm, "end": v(-27.27, 4.65) * mm});
            skLineSegment(sketch, "E330", {"start": v(-27.27, 4.65) * mm, "end": v(-27.05, 4.94) * mm});
            skLineSegment(sketch, "E331", {"start": v(-27.05, 4.94) * mm, "end": v(-26.84, 5.24) * mm});
            skLineSegment(sketch, "E332", {"start": v(-26.84, 5.24) * mm, "end": v(-26.61, 5.53) * mm});
            skLineSegment(sketch, "E333", {"start": v(-26.61, 5.53) * mm, "end": v(-26.83, 5.6) * mm});
            skLineSegment(sketch, "E334", {"start": v(-26.83, 5.6) * mm, "end": v(-26.8, 5.8) * mm});
            skLineSegment(sketch, "E335", {"start": v(-26.8, 5.8) * mm, "end": v(-26.8, 6) * mm});
            skLineSegment(sketch, "E336", {"start": v(-26.8, 6) * mm, "end": v(-26.66, 6.2) * mm});
            skLineSegment(sketch, "E337", {"start": v(-26.66, 6.2) * mm, "end": v(-26.46, 6.36) * mm});
            skLineSegment(sketch, "E338", {"start": v(-26.46, 6.36) * mm, "end": v(-25, 7.16) * mm});
            skLineSegment(sketch, "E339", {"start": v(-25, 7.16) * mm, "end": v(-24.77, 7.33) * mm});
            skLineSegment(sketch, "E340", {"start": v(-24.77, 7.33) * mm, "end": v(-24.56, 7.54) * mm});
            skLineSegment(sketch, "E341", {"start": v(-24.56, 7.54) * mm, "end": v(-23.62, 8.43) * mm});
            skLineSegment(sketch, "E342", {"start": v(-23.62, 8.43) * mm, "end": v(-22.64, 9.27) * mm});
            skLineSegment(sketch, "E343", {"start": v(-22.64, 9.27) * mm, "end": v(-22.28, 9.54) * mm});
            skLineSegment(sketch, "E344", {"start": v(-22.28, 9.54) * mm, "end": v(-21.97, 9.85) * mm});
            skLineSegment(sketch, "E345", {"start": v(-21.97, 9.85) * mm, "end": v(-21.68, 10.2) * mm});
            skLineSegment(sketch, "E346", {"start": v(-21.68, 10.2) * mm, "end": v(-21.4, 10.56) * mm});
            skLineSegment(sketch, "E347", {"start": v(-21.4, 10.56) * mm, "end": v(-21.1, 10.97) * mm});
            skLineSegment(sketch, "E348", {"start": v(-21.1, 10.97) * mm, "end": v(-20.8, 11.39) * mm});
            skLineSegment(sketch, "E349", {"start": v(-20.8, 11.39) * mm, "end": v(-20.49, 11.79) * mm});
            skLineSegment(sketch, "E350", {"start": v(-20.49, 11.79) * mm, "end": v(-20.13, 12.16) * mm});
            skLineSegment(sketch, "E351", {"start": v(-20.13, 12.16) * mm, "end": v(-19.5, 12.7) * mm});
            skLineSegment(sketch, "E352", {"start": v(-19.5, 12.7) * mm, "end": v(-18.8, 13.15) * mm});
            skLineSegment(sketch, "E353", {"start": v(-18.8, 13.15) * mm, "end": v(-18.26, 13.3) * mm});
            skLineSegment(sketch, "E354", {"start": v(-18.26, 13.3) * mm, "end": v(-17.7, 13.38) * mm});
            skLineSegment(sketch, "E355", {"start": v(-17.7, 13.38) * mm, "end": v(-17.13, 13.42) * mm});
            skLineSegment(sketch, "E356", {"start": v(-17.13, 13.42) * mm, "end": v(-16.57, 13.47) * mm});
            skLineSegment(sketch, "E357", {"start": v(-16.57, 13.47) * mm, "end": v(-15.97, 13.73) * mm});
            skLineSegment(sketch, "E358", {"start": v(-15.97, 13.73) * mm, "end": v(-15.35, 13.9) * mm});
            skLineSegment(sketch, "E359", {"start": v(-15.35, 13.9) * mm, "end": v(-13.45, 14.26) * mm});
            skLineSegment(sketch, "E360", {"start": v(-13.45, 14.26) * mm, "end": v(-12.36, 14.3) * mm});
            skLineSegment(sketch, "E361", {"start": v(-12.36, 14.3) * mm, "end": v(-11.27, 14.34) * mm});
            skLineSegment(sketch, "E362", {"start": v(-11.27, 14.34) * mm, "end": v(-11.58, 14.48) * mm});
            skLineSegment(sketch, "E363", {"start": v(-11.58, 14.48) * mm, "end": v(-11.88, 14.64) * mm});
            skLineSegment(sketch, "E364", {"start": v(-6.2, 10.63) * mm, "end": v(-6.15, 10.82) * mm});
            skLineSegment(sketch, "E365", {"start": v(-6.15, 10.82) * mm, "end": v(-6.06, 11) * mm});
            skLineSegment(sketch, "E366", {"start": v(-6.06, 11) * mm, "end": v(-5.96, 11.17) * mm});
            skLineSegment(sketch, "E367", {"start": v(-5.96, 11.17) * mm, "end": v(-5.85, 11.34) * mm});
            skLineSegment(sketch, "E368", {"start": v(-5.85, 11.34) * mm, "end": v(-5.67, 11.27) * mm});
            skLineSegment(sketch, "E369", {"start": v(-5.67, 11.27) * mm, "end": v(-5.5, 11.18) * mm});
            skLineSegment(sketch, "E370", {"start": v(-5.5, 11.18) * mm, "end": v(-5.35, 11.06) * mm});
            skLineSegment(sketch, "E371", {"start": v(-5.35, 11.06) * mm, "end": v(-5.24, 10.9) * mm});
            skLineSegment(sketch, "E372", {"start": v(-5.24, 10.9) * mm, "end": v(-5.17, 10.73) * mm});
            skLineSegment(sketch, "E373", {"start": v(-5.17, 10.73) * mm, "end": v(-5.16, 10.56) * mm});
            skLineSegment(sketch, "E374", {"start": v(-5.16, 10.56) * mm, "end": v(-5.17, 10.38) * mm});
            skLineSegment(sketch, "E375", {"start": v(-5.17, 10.38) * mm, "end": v(-5.22, 10.2) * mm});
            skLineSegment(sketch, "E376", {"start": v(-5.22, 10.2) * mm, "end": v(-5.28, 10.1) * mm});
            skLineSegment(sketch, "E377", {"start": v(-5.28, 10.1) * mm, "end": v(-5.36, 10.02) * mm});
            skLineSegment(sketch, "E378", {"start": v(-5.36, 10.02) * mm, "end": v(-5.47, 9.97) * mm});
            skLineSegment(sketch, "E379", {"start": v(-5.47, 9.97) * mm, "end": v(-5.59, 9.97) * mm});
            skLineSegment(sketch, "E380", {"start": v(-5.59, 9.97) * mm, "end": v(-5.8, 10.06) * mm});
            skLineSegment(sketch, "E381", {"start": v(-5.8, 10.06) * mm, "end": v(-6, 10.2) * mm});
            skLineSegment(sketch, "E382", {"start": v(-6, 10.2) * mm, "end": v(-6.13, 10.4) * mm});
            skLineSegment(sketch, "E383", {"start": v(-6.13, 10.4) * mm, "end": v(-6.2, 10.63) * mm});
            skLineSegment(sketch, "E384", {"start": v(-5.84, 10.61) * mm, "end": v(-5.8, 10.7) * mm});
            skLineSegment(sketch, "E385", {"start": v(-5.8, 10.7) * mm, "end": v(-5.72, 10.76) * mm});
            skLineSegment(sketch, "E386", {"start": v(-5.72, 10.76) * mm, "end": v(-5.63, 10.8) * mm});
            skLineSegment(sketch, "E387", {"start": v(-5.63, 10.8) * mm, "end": v(-5.55, 10.84) * mm});
            skLineSegment(sketch, "E388", {"start": v(-5.55, 10.84) * mm, "end": v(-5.46, 10.78) * mm});
            skLineSegment(sketch, "E389", {"start": v(-5.46, 10.78) * mm, "end": v(-5.38, 10.72) * mm});
            skLineSegment(sketch, "E390", {"start": v(-5.38, 10.72) * mm, "end": v(-5.33, 10.63) * mm});
            skLineSegment(sketch, "E391", {"start": v(-5.33, 10.63) * mm, "end": v(-5.34, 10.53) * mm});
            skLineSegment(sketch, "E392", {"start": v(-5.34, 10.53) * mm, "end": v(-5.4, 10.4) * mm});
            skLineSegment(sketch, "E393", {"start": v(-5.4, 10.4) * mm, "end": v(-5.5, 10.3) * mm});
            skLineSegment(sketch, "E394", {"start": v(-5.5, 10.3) * mm, "end": v(-5.63, 10.24) * mm});
            skLineSegment(sketch, "E395", {"start": v(-5.63, 10.24) * mm, "end": v(-5.77, 10.25) * mm});
            skLineSegment(sketch, "E396", {"start": v(-5.77, 10.25) * mm, "end": v(-5.84, 10.32) * mm});
            skLineSegment(sketch, "E397", {"start": v(-5.84, 10.32) * mm, "end": v(-5.86, 10.41) * mm});
            skLineSegment(sketch, "E398", {"start": v(-5.86, 10.41) * mm, "end": v(-5.86, 10.52) * mm});
            skLineSegment(sketch, "E399", {"start": v(-5.86, 10.52) * mm, "end": v(-5.84, 10.61) * mm});
            skLineSegment(sketch, "E400", {"start": v(6.14, 9) * mm, "end": v(6.34, 9.15) * mm});
            skLineSegment(sketch, "E401", {"start": v(6.34, 9.15) * mm, "end": v(6.56, 9.27) * mm});
            skLineSegment(sketch, "E402", {"start": v(6.56, 9.27) * mm, "end": v(6.8, 9.35) * mm});
            skLineSegment(sketch, "E403", {"start": v(6.8, 9.35) * mm, "end": v(7.04, 9.35) * mm});
            skLineSegment(sketch, "E404", {"start": v(7.04, 9.35) * mm, "end": v(9.05, 8.97) * mm});
            skLineSegment(sketch, "E405", {"start": v(9.05, 8.97) * mm, "end": v(11.04, 8.51) * mm});
            skLineSegment(sketch, "E406", {"start": v(11.04, 8.51) * mm, "end": v(11.3, 8.4) * mm});
            skLineSegment(sketch, "E407", {"start": v(11.3, 8.4) * mm, "end": v(11.52, 8.25) * mm});
            skLineSegment(sketch, "E408", {"start": v(11.52, 8.25) * mm, "end": v(11.72, 8.04) * mm});
            skLineSegment(sketch, "E409", {"start": v(11.72, 8.04) * mm, "end": v(11.89, 7.82) * mm});
            skLineSegment(sketch, "E410", {"start": v(11.89, 7.82) * mm, "end": v(12.21, 7.03) * mm});
            skLineSegment(sketch, "E411", {"start": v(12.21, 7.03) * mm, "end": v(12.37, 6.2) * mm});
            skLineSegment(sketch, "E412", {"start": v(12.37, 6.2) * mm, "end": v(12.37, 5.86) * mm});
            skLineSegment(sketch, "E413", {"start": v(12.37, 5.86) * mm, "end": v(12.27, 5.55) * mm});
            skLineSegment(sketch, "E414", {"start": v(12.27, 5.55) * mm, "end": v(12.1, 5.27) * mm});
            skLineSegment(sketch, "E415", {"start": v(12.1, 5.27) * mm, "end": v(11.88, 5.02) * mm});
            skLineSegment(sketch, "E416", {"start": v(11.88, 5.02) * mm, "end": v(11.5, 6.56) * mm});
            skLineSegment(sketch, "E417", {"start": v(11.5, 6.56) * mm, "end": v(11.37, 7.03) * mm});
            skLineSegment(sketch, "E418", {"start": v(11.37, 7.03) * mm, "end": v(11.18, 7.47) * mm});
            skLineSegment(sketch, "E419", {"start": v(11.18, 7.47) * mm, "end": v(11.05, 7.63) * mm});
            skLineSegment(sketch, "E420", {"start": v(11.05, 7.63) * mm, "end": v(10.9, 7.77) * mm});
            skLineSegment(sketch, "E421", {"start": v(10.9, 7.77) * mm, "end": v(10.72, 7.87) * mm});
            skLineSegment(sketch, "E422", {"start": v(10.72, 7.87) * mm, "end": v(10.52, 7.94) * mm});
            skLineSegment(sketch, "E423", {"start": v(10.52, 7.94) * mm, "end": v(6.14, 9) * mm});
            skLineSegment(sketch, "E424", {"start": v(5.49, 8.5) * mm, "end": v(5.81, 8.74) * mm});
            skLineSegment(sketch, "E425", {"start": v(5.81, 8.74) * mm, "end": v(10, 7.68) * mm});
            skLineSegment(sketch, "E426", {"start": v(10, 7.68) * mm, "end": v(10.34, 7.54) * mm});
            skLineSegment(sketch, "E427", {"start": v(10.34, 7.54) * mm, "end": v(10.63, 7.32) * mm});
            skLineSegment(sketch, "E428", {"start": v(10.63, 7.32) * mm, "end": v(10.86, 7.03) * mm});
            skLineSegment(sketch, "E429", {"start": v(10.86, 7.03) * mm, "end": v(11.03, 6.7) * mm});
            skLineSegment(sketch, "E430", {"start": v(11.03, 6.7) * mm, "end": v(11.33, 5.82) * mm});
            skLineSegment(sketch, "E431", {"start": v(11.33, 5.82) * mm, "end": v(11.56, 4.92) * mm});
            skLineSegment(sketch, "E432", {"start": v(11.56, 4.92) * mm, "end": v(11.56, 4.77) * mm});
            skLineSegment(sketch, "E433", {"start": v(11.56, 4.77) * mm, "end": v(11.5, 4.63) * mm});
            skLineSegment(sketch, "E434", {"start": v(11.5, 4.63) * mm, "end": v(11.41, 4.51) * mm});
            skLineSegment(sketch, "E435", {"start": v(11.41, 4.51) * mm, "end": v(11.32, 4.4) * mm});
            skLineSegment(sketch, "E436", {"start": v(11.32, 4.4) * mm, "end": v(11.07, 5.32) * mm});
            skLineSegment(sketch, "E437", {"start": v(11.07, 5.32) * mm, "end": v(10.83, 6.26) * mm});
            skLineSegment(sketch, "E438", {"start": v(10.83, 6.26) * mm, "end": v(10.65, 6.76) * mm});
            skLineSegment(sketch, "E439", {"start": v(10.65, 6.76) * mm, "end": v(10.3, 7.16) * mm});
            skLineSegment(sketch, "E440", {"start": v(10.3, 7.16) * mm, "end": v(9.85, 7.4) * mm});
            skLineSegment(sketch, "E441", {"start": v(9.85, 7.4) * mm, "end": v(9.35, 7.54) * mm});
            skLineSegment(sketch, "E442", {"start": v(9.35, 7.54) * mm, "end": v(5.49, 8.5) * mm});
            skLineSegment(sketch, "E443", {"start": v(4.93, 7.98) * mm, "end": v(5.24, 8.27) * mm});
            skLineSegment(sketch, "E444", {"start": v(5.24, 8.27) * mm, "end": v(7.4, 7.71) * mm});
            skLineSegment(sketch, "E445", {"start": v(7.4, 7.71) * mm, "end": v(9.53, 7.11) * mm});
            skLineSegment(sketch, "E446", {"start": v(9.53, 7.11) * mm, "end": v(9.83, 6.98) * mm});
            skLineSegment(sketch, "E447", {"start": v(9.83, 6.98) * mm, "end": v(10.08, 6.76) * mm});
            skLineSegment(sketch, "E448", {"start": v(10.08, 6.76) * mm, "end": v(10.27, 6.48) * mm});
            skLineSegment(sketch, "E449", {"start": v(10.27, 6.48) * mm, "end": v(10.4, 6.18) * mm});
            skLineSegment(sketch, "E450", {"start": v(10.4, 6.18) * mm, "end": v(10.7, 5.23) * mm});
            skLineSegment(sketch, "E451", {"start": v(10.7, 5.23) * mm, "end": v(10.94, 4.25) * mm});
            skLineSegment(sketch, "E452", {"start": v(10.94, 4.25) * mm, "end": v(10.94, 4.11) * mm});
            skLineSegment(sketch, "E453", {"start": v(10.94, 4.11) * mm, "end": v(10.9, 3.98) * mm});
            skLineSegment(sketch, "E454", {"start": v(10.9, 3.98) * mm, "end": v(10.84, 3.85) * mm});
            skLineSegment(sketch, "E455", {"start": v(10.84, 3.85) * mm, "end": v(10.77, 3.73) * mm});
            skLineSegment(sketch, "E456", {"start": v(10.77, 3.73) * mm, "end": v(10.26, 5.57) * mm});
            skLineSegment(sketch, "E457", {"start": v(10.26, 5.57) * mm, "end": v(10.15, 5.94) * mm});
            skLineSegment(sketch, "E458", {"start": v(10.15, 5.94) * mm, "end": v(10, 6.3) * mm});
            skLineSegment(sketch, "E459", {"start": v(10, 6.3) * mm, "end": v(9.84, 6.5) * mm});
            skLineSegment(sketch, "E460", {"start": v(9.84, 6.5) * mm, "end": v(9.64, 6.65) * mm});
            skLineSegment(sketch, "E461", {"start": v(9.64, 6.65) * mm, "end": v(9.42, 6.77) * mm});
            skLineSegment(sketch, "E462", {"start": v(9.42, 6.77) * mm, "end": v(9.18, 6.85) * mm});
            skLineSegment(sketch, "E463", {"start": v(9.18, 6.85) * mm, "end": v(4.93, 7.98) * mm});
            skLineSegment(sketch, "E464", {"start": v(4.3, 7.47) * mm, "end": v(4.67, 7.76) * mm});
            skLineSegment(sketch, "E465", {"start": v(4.67, 7.76) * mm, "end": v(9.04, 6.52) * mm});
            skLineSegment(sketch, "E466", {"start": v(9.04, 6.52) * mm, "end": v(9.23, 6.44) * mm});
            skLineSegment(sketch, "E467", {"start": v(9.23, 6.44) * mm, "end": v(9.41, 6.33) * mm});
            skLineSegment(sketch, "E468", {"start": v(9.41, 6.33) * mm, "end": v(9.57, 6.2) * mm});
            skLineSegment(sketch, "E469", {"start": v(9.57, 6.2) * mm, "end": v(9.68, 6.02) * mm});
            skLineSegment(sketch, "E470", {"start": v(9.68, 6.02) * mm, "end": v(10.12, 4.74) * mm});
            skLineSegment(sketch, "E471", {"start": v(10.12, 4.74) * mm, "end": v(10.52, 3.44) * mm});
            skLineSegment(sketch, "E472", {"start": v(10.52, 3.44) * mm, "end": v(10.3, 3.2) * mm});
            skLineSegment(sketch, "E473", {"start": v(10.3, 3.2) * mm, "end": v(9.32, 5.71) * mm});
            skLineSegment(sketch, "E474", {"start": v(9.32, 5.71) * mm, "end": v(9.25, 5.84) * mm});
            skLineSegment(sketch, "E475", {"start": v(9.25, 5.84) * mm, "end": v(9.15, 5.94) * mm});
            skLineSegment(sketch, "E476", {"start": v(9.15, 5.94) * mm, "end": v(9.03, 6.01) * mm});
            skLineSegment(sketch, "E477", {"start": v(9.03, 6.01) * mm, "end": v(8.9, 6.06) * mm});
            skLineSegment(sketch, "E478", {"start": v(8.9, 6.06) * mm, "end": v(4.3, 7.47) * mm});
            skLineSegment(sketch, "E479", {"start": v(3.77, 7.02) * mm, "end": v(3.85, 7.1) * mm});
            skLineSegment(sketch, "E480", {"start": v(3.85, 7.1) * mm, "end": v(3.94, 7.17) * mm});
            skLineSegment(sketch, "E481", {"start": v(3.94, 7.17) * mm, "end": v(4.03, 7.23) * mm});
            skLineSegment(sketch, "E482", {"start": v(4.03, 7.23) * mm, "end": v(4.14, 7.22) * mm});
            skLineSegment(sketch, "E483", {"start": v(4.14, 7.22) * mm, "end": v(8.14, 6.02) * mm});
            skLineSegment(sketch, "E484", {"start": v(8.14, 6.02) * mm, "end": v(8.46, 5.92) * mm});
            skLineSegment(sketch, "E485", {"start": v(8.46, 5.92) * mm, "end": v(8.77, 5.78) * mm});
            skLineSegment(sketch, "E486", {"start": v(8.77, 5.78) * mm, "end": v(8.92, 5.64) * mm});
            skLineSegment(sketch, "E487", {"start": v(8.92, 5.64) * mm, "end": v(9.05, 5.48) * mm});
            skLineSegment(sketch, "E488", {"start": v(9.05, 5.48) * mm, "end": v(9.15, 5.3) * mm});
            skLineSegment(sketch, "E489", {"start": v(9.15, 5.3) * mm, "end": v(9.23, 5.11) * mm});
            skLineSegment(sketch, "E490", {"start": v(9.23, 5.11) * mm, "end": v(9.48, 4.1) * mm});
            skLineSegment(sketch, "E491", {"start": v(9.48, 4.1) * mm, "end": v(9.35, 4.03) * mm});
            skLineSegment(sketch, "E492", {"start": v(9.35, 4.03) * mm, "end": v(9.2, 3.98) * mm});
            skLineSegment(sketch, "E493", {"start": v(9.2, 3.98) * mm, "end": v(9.05, 4.5) * mm});
            skLineSegment(sketch, "E494", {"start": v(9.05, 4.5) * mm, "end": v(8.86, 5) * mm});
            skLineSegment(sketch, "E495", {"start": v(8.86, 5) * mm, "end": v(8.68, 5.26) * mm});
            skLineSegment(sketch, "E496", {"start": v(8.68, 5.26) * mm, "end": v(8.44, 5.48) * mm});
            skLineSegment(sketch, "E497", {"start": v(8.44, 5.48) * mm, "end": v(8.17, 5.64) * mm});
            skLineSegment(sketch, "E498", {"start": v(8.17, 5.64) * mm, "end": v(7.87, 5.76) * mm});
            skLineSegment(sketch, "E499", {"start": v(7.87, 5.76) * mm, "end": v(3.77, 7.02) * mm});
            skLineSegment(sketch, "E500", {"start": v(3.06, 6.47) * mm, "end": v(3.44, 6.73) * mm});
            skLineSegment(sketch, "E501", {"start": v(3.44, 6.73) * mm, "end": v(7.73, 5.41) * mm});
            skLineSegment(sketch, "E502", {"start": v(7.73, 5.41) * mm, "end": v(7.97, 5.32) * mm});
            skLineSegment(sketch, "E503", {"start": v(7.97, 5.32) * mm, "end": v(8.18, 5.18) * mm});
            skLineSegment(sketch, "E504", {"start": v(8.18, 5.18) * mm, "end": v(8.36, 5.01) * mm});
            skLineSegment(sketch, "E505", {"start": v(8.36, 5.01) * mm, "end": v(8.5, 4.8) * mm});
            skLineSegment(sketch, "E506", {"start": v(8.5, 4.8) * mm, "end": v(8.6, 4.6) * mm});
            skLineSegment(sketch, "E507", {"start": v(8.6, 4.6) * mm, "end": v(8.67, 4.38) * mm});
            skLineSegment(sketch, "E508", {"start": v(8.67, 4.38) * mm, "end": v(8.69, 4.16) * mm});
            skLineSegment(sketch, "E509", {"start": v(8.69, 4.16) * mm, "end": v(8.63, 3.94) * mm});
            skLineSegment(sketch, "E510", {"start": v(8.63, 3.94) * mm, "end": v(8.54, 3.92) * mm});
            skLineSegment(sketch, "E511", {"start": v(8.54, 3.92) * mm, "end": v(8.46, 3.91) * mm});
            skLineSegment(sketch, "E512", {"start": v(8.46, 3.91) * mm, "end": v(8.27, 4.42) * mm});
            skLineSegment(sketch, "E513", {"start": v(8.27, 4.42) * mm, "end": v(7.93, 4.84) * mm});
            skLineSegment(sketch, "E514", {"start": v(7.93, 4.84) * mm, "end": v(7.6, 5.07) * mm});
            skLineSegment(sketch, "E515", {"start": v(7.6, 5.07) * mm, "end": v(7.21, 5.22) * mm});
            skLineSegment(sketch, "E516", {"start": v(7.21, 5.22) * mm, "end": v(6.82, 5.33) * mm});
            skLineSegment(sketch, "E517", {"start": v(6.82, 5.33) * mm, "end": v(6.43, 5.44) * mm});
            skLineSegment(sketch, "E518", {"start": v(6.43, 5.44) * mm, "end": v(3.06, 6.47) * mm});
            skLineSegment(sketch, "E519", {"start": v(2.11, 5.7) * mm, "end": v(2.35, 5.86) * mm});
            skLineSegment(sketch, "E520", {"start": v(2.35, 5.86) * mm, "end": v(2.63, 5.97) * mm});
            skLineSegment(sketch, "E521", {"start": v(2.63, 5.97) * mm, "end": v(2.92, 6) * mm});
            skLineSegment(sketch, "E522", {"start": v(2.92, 6) * mm, "end": v(3.2, 5.97) * mm});
            skLineSegment(sketch, "E523", {"start": v(3.2, 5.97) * mm, "end": v(7.08, 4.86) * mm});
            skLineSegment(sketch, "E524", {"start": v(7.08, 4.86) * mm, "end": v(7.35, 4.75) * mm});
            skLineSegment(sketch, "E525", {"start": v(7.35, 4.75) * mm, "end": v(7.6, 4.6) * mm});
            skLineSegment(sketch, "E526", {"start": v(7.6, 4.6) * mm, "end": v(7.8, 4.4) * mm});
            skLineSegment(sketch, "E527", {"start": v(7.8, 4.4) * mm, "end": v(7.95, 4.14) * mm});
            skLineSegment(sketch, "E528", {"start": v(7.95, 4.14) * mm, "end": v(8.02, 3.56) * mm});
            skLineSegment(sketch, "E529", {"start": v(8.02, 3.56) * mm, "end": v(7.9, 3) * mm});
            skLineSegment(sketch, "E530", {"start": v(7.9, 3) * mm, "end": v(7.82, 2.64) * mm});
            skLineSegment(sketch, "E531", {"start": v(7.82, 2.64) * mm, "end": v(7.8, 2.28) * mm});
            skLineSegment(sketch, "E532", {"start": v(7.8, 2.28) * mm, "end": v(7.84, 1.92) * mm});
            skLineSegment(sketch, "E533", {"start": v(7.84, 1.92) * mm, "end": v(7.96, 1.58) * mm});
            skLineSegment(sketch, "E534", {"start": v(7.96, 1.58) * mm, "end": v(8.15, 1.28) * mm});
            skLineSegment(sketch, "E535", {"start": v(8.15, 1.28) * mm, "end": v(8.4, 1.01) * mm});
            skLineSegment(sketch, "E536", {"start": v(8.4, 1.01) * mm, "end": v(7.35, -0.18) * mm});
            skLineSegment(sketch, "E537", {"start": v(7.35, -0.18) * mm, "end": v(6.27, -1.34) * mm});
            skLineSegment(sketch, "E538", {"start": v(6.27, -1.34) * mm, "end": v(6.07, -1.53) * mm});
            skLineSegment(sketch, "E539", {"start": v(6.07, -1.53) * mm, "end": v(5.84, -1.68) * mm});
            skLineSegment(sketch, "E540", {"start": v(5.84, -1.68) * mm, "end": v(5.35, -1.8) * mm});
            skLineSegment(sketch, "E541", {"start": v(5.35, -1.8) * mm, "end": v(4.86, -1.73) * mm});
            skLineSegment(sketch, "E542", {"start": v(4.86, -1.73) * mm, "end": v(2.59, -0.8) * mm});
            skLineSegment(sketch, "E543", {"start": v(2.59, -0.8) * mm, "end": v(0.37, 0.26) * mm});
            skLineSegment(sketch, "E544", {"start": v(0.37, 0.26) * mm, "end": v(0.01, 0.54) * mm});
            skLineSegment(sketch, "E545", {"start": v(0.01, 0.54) * mm, "end": v(-0.26, 0.9) * mm});
            skLineSegment(sketch, "E546", {"start": v(-0.26, 0.9) * mm, "end": v(-0.46, 1.32) * mm});
            skLineSegment(sketch, "E547", {"start": v(-0.46, 1.32) * mm, "end": v(-0.6, 1.76) * mm});
            skLineSegment(sketch, "E548", {"start": v(-0.6, 1.76) * mm, "end": v(-0.7, 2.23) * mm});
            skLineSegment(sketch, "E549", {"start": v(-0.7, 2.23) * mm, "end": v(-0.77, 2.71) * mm});
            skLineSegment(sketch, "E550", {"start": v(-0.77, 2.71) * mm, "end": v(-0.7, 2.98) * mm});
            skLineSegment(sketch, "E551", {"start": v(-0.7, 2.98) * mm, "end": v(-0.56, 3.22) * mm});
            skLineSegment(sketch, "E552", {"start": v(-0.56, 3.22) * mm, "end": v(-0.39, 3.44) * mm});
            skLineSegment(sketch, "E553", {"start": v(-0.39, 3.44) * mm, "end": v(-0.21, 3.65) * mm});
            skLineSegment(sketch, "E554", {"start": v(-0.21, 3.65) * mm, "end": v(0.91, 4.71) * mm});
            skLineSegment(sketch, "E555", {"start": v(0.91, 4.71) * mm, "end": v(2.11, 5.7) * mm});
            skLineSegment(sketch, "E556", {"start": v(8.25, 2.94) * mm, "end": v(8.45, 3.22) * mm});
            skLineSegment(sketch, "E557", {"start": v(8.45, 3.22) * mm, "end": v(8.71, 3.42) * mm});
            skLineSegment(sketch, "E558", {"start": v(8.71, 3.42) * mm, "end": v(9.02, 3.55) * mm});
            skLineSegment(sketch, "E559", {"start": v(9.02, 3.55) * mm, "end": v(9.35, 3.6) * mm});
            skLineSegment(sketch, "E560", {"start": v(9.35, 3.6) * mm, "end": v(9.48, 3.58) * mm});
            skLineSegment(sketch, "E561", {"start": v(9.48, 3.58) * mm, "end": v(9.6, 3.52) * mm});
            skLineSegment(sketch, "E562", {"start": v(9.6, 3.52) * mm, "end": v(9.69, 3.43) * mm});
            skLineSegment(sketch, "E563", {"start": v(9.69, 3.43) * mm, "end": v(9.76, 3.33) * mm});
            skLineSegment(sketch, "E564", {"start": v(9.76, 3.33) * mm, "end": v(9.86, 3.16) * mm});
            skLineSegment(sketch, "E565", {"start": v(9.86, 3.16) * mm, "end": v(9.92, 2.97) * mm});
            skLineSegment(sketch, "E566", {"start": v(9.92, 2.97) * mm, "end": v(9.94, 2.78) * mm});
            skLineSegment(sketch, "E567", {"start": v(9.94, 2.78) * mm, "end": v(9.9, 2.58) * mm});
            skLineSegment(sketch, "E568", {"start": v(9.9, 2.58) * mm, "end": v(9.71, 1.72) * mm});
            skLineSegment(sketch, "E569", {"start": v(9.71, 1.72) * mm, "end": v(9.63, 0.84) * mm});
            skLineSegment(sketch, "E570", {"start": v(9.63, 0.84) * mm, "end": v(9.6, -0.05) * mm});
            skLineSegment(sketch, "E571", {"start": v(9.6, -0.05) * mm, "end": v(9.62, -0.93) * mm});
            skLineSegment(sketch, "E572", {"start": v(9.62, -0.93) * mm, "end": v(9.62, -2.39) * mm});
            skLineSegment(sketch, "E573", {"start": v(9.62, -2.39) * mm, "end": v(9.49, -3.84) * mm});
            skLineSegment(sketch, "E574", {"start": v(9.49, -3.84) * mm, "end": v(9.4, -4.28) * mm});
            skLineSegment(sketch, "E575", {"start": v(9.4, -4.28) * mm, "end": v(9.2, -4.7) * mm});
            skLineSegment(sketch, "E576", {"start": v(9.2, -4.7) * mm, "end": v(8.86, -5) * mm});
            skLineSegment(sketch, "E577", {"start": v(8.86, -5) * mm, "end": v(8.43, -5.2) * mm});
            skLineSegment(sketch, "E578", {"start": v(8.43, -5.2) * mm, "end": v(7.96, -5.27) * mm});
            skLineSegment(sketch, "E579", {"start": v(7.96, -5.27) * mm, "end": v(7.49, -5.21) * mm});
            skLineSegment(sketch, "E580", {"start": v(7.49, -5.21) * mm, "end": v(5.68, -4.63) * mm});
            skLineSegment(sketch, "E581", {"start": v(5.68, -4.63) * mm, "end": v(5.68, -5.4) * mm});
            skLineSegment(sketch, "E582", {"start": v(5.68, -5.4) * mm, "end": v(7.08, -5.7) * mm});
            skLineSegment(sketch, "E583", {"start": v(7.08, -5.7) * mm, "end": v(8.43, -6.17) * mm});
            skLineSegment(sketch, "E584", {"start": v(8.43, -6.17) * mm, "end": v(8.56, -6.21) * mm});
            skLineSegment(sketch, "E585", {"start": v(8.56, -6.21) * mm, "end": v(8.7, -6.21) * mm});
            skLineSegment(sketch, "E586", {"start": v(8.7, -6.21) * mm, "end": v(8.85, -6.2) * mm});
            skLineSegment(sketch, "E587", {"start": v(8.85, -6.2) * mm, "end": v(9, -6.18) * mm});
            skLineSegment(sketch, "E588", {"start": v(9, -6.18) * mm, "end": v(11.76, -5.86) * mm});
            skLineSegment(sketch, "E589", {"start": v(11.76, -5.86) * mm, "end": v(13.04, -5.66) * mm});
            skLineSegment(sketch, "E590", {"start": v(13.04, -5.66) * mm, "end": v(14.3, -5.47) * mm});
            skLineSegment(sketch, "E591", {"start": v(14.3, -5.47) * mm, "end": v(16.24, -5.25) * mm});
            skLineSegment(sketch, "E592", {"start": v(16.24, -5.25) * mm, "end": v(18.18, -5.12) * mm});
            skLineSegment(sketch, "E593", {"start": v(18.18, -5.12) * mm, "end": v(19.06, -5.15) * mm});
            skLineSegment(sketch, "E594", {"start": v(19.06, -5.15) * mm, "end": v(19.22, -5.2) * mm});
            skLineSegment(sketch, "E595", {"start": v(19.22, -5.2) * mm, "end": v(19.33, -5.3) * mm});
            skLineSegment(sketch, "E596", {"start": v(19.33, -5.3) * mm, "end": v(19.37, -5.4) * mm});
            skLineSegment(sketch, "E597", {"start": v(19.37, -5.4) * mm, "end": v(19.35, -5.52) * mm});
            skLineSegment(sketch, "E598", {"start": v(19.35, -5.52) * mm, "end": v(19.28, -5.61) * mm});
            skLineSegment(sketch, "E599", {"start": v(19.28, -5.61) * mm, "end": v(19.2, -5.68) * mm});
            skLineSegment(sketch, "E600", {"start": v(19.2, -5.68) * mm, "end": v(18.77, -5.86) * mm});
            skLineSegment(sketch, "E601", {"start": v(18.77, -5.86) * mm, "end": v(18.33, -6) * mm});
            skLineSegment(sketch, "E602", {"start": v(18.33, -6) * mm, "end": v(17.61, -6.24) * mm});
            skLineSegment(sketch, "E603", {"start": v(17.61, -6.24) * mm, "end": v(16.9, -6.5) * mm});
            skLineSegment(sketch, "E604", {"start": v(16.9, -6.5) * mm, "end": v(19.14, -6.37) * mm});
            skLineSegment(sketch, "E605", {"start": v(19.14, -6.37) * mm, "end": v(21.38, -6.27) * mm});
            skLineSegment(sketch, "E606", {"start": v(21.38, -6.27) * mm, "end": v(22.87, -6.22) * mm});
            skLineSegment(sketch, "E607", {"start": v(22.87, -6.22) * mm, "end": v(23.93, -6.23) * mm});
            skLineSegment(sketch, "E608", {"start": v(23.93, -6.23) * mm, "end": v(24.99, -6.32) * mm});
            skLineSegment(sketch, "E609", {"start": v(24.99, -6.32) * mm, "end": v(25.13, -6.35) * mm});
            skLineSegment(sketch, "E610", {"start": v(25.13, -6.35) * mm, "end": v(25.26, -6.41) * mm});
            skLineSegment(sketch, "E611", {"start": v(25.26, -6.41) * mm, "end": v(25.36, -6.5) * mm});
            skLineSegment(sketch, "E612", {"start": v(25.36, -6.5) * mm, "end": v(25.4, -6.64) * mm});
            skLineSegment(sketch, "E613", {"start": v(25.4, -6.64) * mm, "end": v(25.4, -6.79) * mm});
            skLineSegment(sketch, "E614", {"start": v(25.4, -6.79) * mm, "end": v(25.3, -6.9) * mm});
            skLineSegment(sketch, "E615", {"start": v(25.3, -6.9) * mm, "end": v(25.18, -7) * mm});
            skLineSegment(sketch, "E616", {"start": v(25.18, -7) * mm, "end": v(25.05, -7.07) * mm});
            skLineSegment(sketch, "E617", {"start": v(25.05, -7.07) * mm, "end": v(25.7, -7.24) * mm});
            skLineSegment(sketch, "E618", {"start": v(25.7, -7.24) * mm, "end": v(26.37, -7.36) * mm});
            skLineSegment(sketch, "E619", {"start": v(26.37, -7.36) * mm, "end": v(28.28, -7.6) * mm});
            skLineSegment(sketch, "E620", {"start": v(28.28, -7.6) * mm, "end": v(30.2, -7.79) * mm});
            skLineSegment(sketch, "E621", {"start": v(30.2, -7.79) * mm, "end": v(32.23, -7.96) * mm});
            skLineSegment(sketch, "E622", {"start": v(32.23, -7.96) * mm, "end": v(34.27, -8.15) * mm});
            skLineSegment(sketch, "E623", {"start": v(34.27, -8.15) * mm, "end": v(33.01, -8.18) * mm});
            skLineSegment(sketch, "E624", {"start": v(33.01, -8.18) * mm, "end": v(31.76, -8.18) * mm});
            skLineSegment(sketch, "E625", {"start": v(31.76, -8.18) * mm, "end": v(28.98, -8.02) * mm});
            skLineSegment(sketch, "E626", {"start": v(28.98, -8.02) * mm, "end": v(26.22, -7.75) * mm});
            skLineSegment(sketch, "E627", {"start": v(26.22, -7.75) * mm, "end": v(25.49, -7.64) * mm});
            skLineSegment(sketch, "E628", {"start": v(25.49, -7.64) * mm, "end": v(24.78, -7.45) * mm});
            skLineSegment(sketch, "E629", {"start": v(24.78, -7.45) * mm, "end": v(24.64, -7.4) * mm});
            skLineSegment(sketch, "E630", {"start": v(24.64, -7.4) * mm, "end": v(24.52, -7.3) * mm});
            skLineSegment(sketch, "E631", {"start": v(24.52, -7.3) * mm, "end": v(24.43, -7.2) * mm});
            skLineSegment(sketch, "E632", {"start": v(24.43, -7.2) * mm, "end": v(24.41, -7.05) * mm});
            skLineSegment(sketch, "E633", {"start": v(24.41, -7.05) * mm, "end": v(24.43, -6.95) * mm});
            skLineSegment(sketch, "E634", {"start": v(24.43, -6.95) * mm, "end": v(24.48, -6.87) * mm});
            skLineSegment(sketch, "E635", {"start": v(24.48, -6.87) * mm, "end": v(24.55, -6.8) * mm});
            skLineSegment(sketch, "E636", {"start": v(24.55, -6.8) * mm, "end": v(24.62, -6.74) * mm});
            skLineSegment(sketch, "E637", {"start": v(24.62, -6.74) * mm, "end": v(23.46, -6.7) * mm});
            skLineSegment(sketch, "E638", {"start": v(23.46, -6.7) * mm, "end": v(22.3, -6.71) * mm});
            skLineSegment(sketch, "E639", {"start": v(22.3, -6.71) * mm, "end": v(18.83, -6.88) * mm});
            skLineSegment(sketch, "E640", {"start": v(18.83, -6.88) * mm, "end": v(15.36, -7.13) * mm});
            skLineSegment(sketch, "E641", {"start": v(15.36, -7.13) * mm, "end": v(15.25, -7.12) * mm});
            skLineSegment(sketch, "E642", {"start": v(15.25, -7.12) * mm, "end": v(15.15, -7.08) * mm});
            skLineSegment(sketch, "E643", {"start": v(15.15, -7.08) * mm, "end": v(15.08, -7) * mm});
            skLineSegment(sketch, "E644", {"start": v(15.08, -7) * mm, "end": v(15.06, -6.9) * mm});
            skLineSegment(sketch, "E645", {"start": v(15.06, -6.9) * mm, "end": v(15.07, -6.78) * mm});
            skLineSegment(sketch, "E646", {"start": v(15.07, -6.78) * mm, "end": v(15.14, -6.69) * mm});
            skLineSegment(sketch, "E647", {"start": v(15.14, -6.69) * mm, "end": v(15.24, -6.62) * mm});
            skLineSegment(sketch, "E648", {"start": v(15.24, -6.62) * mm, "end": v(15.35, -6.57) * mm});
            skLineSegment(sketch, "E649", {"start": v(15.35, -6.57) * mm, "end": v(16.85, -6.03) * mm});
            skLineSegment(sketch, "E650", {"start": v(16.85, -6.03) * mm, "end": v(18.36, -5.52) * mm});
            skLineSegment(sketch, "E651", {"start": v(18.36, -5.52) * mm, "end": v(17.55, -5.52) * mm});
            skLineSegment(sketch, "E652", {"start": v(17.55, -5.52) * mm, "end": v(16.75, -5.56) * mm});
            skLineSegment(sketch, "E653", {"start": v(16.75, -5.56) * mm, "end": v(14.44, -5.76) * mm});
            skLineSegment(sketch, "E654", {"start": v(14.44, -5.76) * mm, "end": v(13.13, -5.91) * mm});
            skLineSegment(sketch, "E655", {"start": v(13.13, -5.91) * mm, "end": v(11.82, -6.07) * mm});
            skLineSegment(sketch, "E656", {"start": v(11.82, -6.07) * mm, "end": v(8.81, -6.31) * mm});
            skLineSegment(sketch, "E657", {"start": v(8.81, -6.31) * mm, "end": v(8.94, -6.42) * mm});
            skLineSegment(sketch, "E658", {"start": v(8.94, -6.42) * mm, "end": v(9.08, -6.5) * mm});
            skLineSegment(sketch, "E659", {"start": v(9.08, -6.5) * mm, "end": v(9.23, -6.58) * mm});
            skLineSegment(sketch, "E660", {"start": v(9.23, -6.58) * mm, "end": v(9.36, -6.68) * mm});
            skLineSegment(sketch, "E661", {"start": v(9.36, -6.68) * mm, "end": v(9.44, -6.76) * mm});
            skLineSegment(sketch, "E662", {"start": v(9.44, -6.76) * mm, "end": v(9.51, -6.86) * mm});
            skLineSegment(sketch, "E663", {"start": v(9.51, -6.86) * mm, "end": v(9.55, -6.96) * mm});
            skLineSegment(sketch, "E664", {"start": v(9.55, -6.96) * mm, "end": v(9.54, -7.08) * mm});
            skLineSegment(sketch, "E665", {"start": v(9.54, -7.08) * mm, "end": v(9.45, -7.19) * mm});
            skLineSegment(sketch, "E666", {"start": v(9.45, -7.19) * mm, "end": v(9.33, -7.26) * mm});
            skLineSegment(sketch, "E667", {"start": v(9.33, -7.26) * mm, "end": v(9.2, -7.32) * mm});
            skLineSegment(sketch, "E668", {"start": v(9.2, -7.32) * mm, "end": v(9.06, -7.37) * mm});
            skLineSegment(sketch, "E669", {"start": v(9.06, -7.37) * mm, "end": v(8.18, -7.53) * mm});
            skLineSegment(sketch, "E670", {"start": v(8.18, -7.53) * mm, "end": v(7.3, -7.6) * mm});
            skLineSegment(sketch, "E671", {"start": v(7.3, -7.6) * mm, "end": v(5.03, -7.61) * mm});
            skLineSegment(sketch, "E672", {"start": v(5.03, -7.61) * mm, "end": v(2.77, -7.48) * mm});
            skLineSegment(sketch, "E673", {"start": v(2.77, -7.48) * mm, "end": v(1.73, -7.37) * mm});
            skLineSegment(sketch, "E674", {"start": v(1.73, -7.37) * mm, "end": v(0.7, -7.18) * mm});
            skLineSegment(sketch, "E675", {"start": v(0.7, -7.18) * mm, "end": v(0.54, -7.13) * mm});
            skLineSegment(sketch, "E676", {"start": v(0.54, -7.13) * mm, "end": v(0.39, -7.07) * mm});
            skLineSegment(sketch, "E677", {"start": v(0.39, -7.07) * mm, "end": v(0.25, -7) * mm});
            skLineSegment(sketch, "E678", {"start": v(0.25, -7) * mm, "end": v(0.12, -6.9) * mm});
            skLineSegment(sketch, "E679", {"start": v(0.12, -6.9) * mm, "end": v(0.62, -6.5) * mm});
            skLineSegment(sketch, "E680", {"start": v(0.62, -6.5) * mm, "end": v(1.17, -6.16) * mm});
            skLineSegment(sketch, "E681", {"start": v(1.17, -6.16) * mm, "end": v(1.76, -5.88) * mm});
            skLineSegment(sketch, "E682", {"start": v(1.76, -5.88) * mm, "end": v(2.36, -5.66) * mm});
            skLineSegment(sketch, "E683", {"start": v(2.36, -5.66) * mm, "end": v(3.23, -5.44) * mm});
            skLineSegment(sketch, "E684", {"start": v(3.23, -5.44) * mm, "end": v(4.12, -5.34) * mm});
            skLineSegment(sketch, "E685", {"start": v(4.12, -5.34) * mm, "end": v(4.16, -5) * mm});
            skLineSegment(sketch, "E686", {"start": v(4.16, -5) * mm, "end": v(4.13, -4.65) * mm});
            skLineSegment(sketch, "E687", {"start": v(4.13, -4.65) * mm, "end": v(4.03, -4.32) * mm});
            skLineSegment(sketch, "E688", {"start": v(4.03, -4.32) * mm, "end": v(3.83, -4.04) * mm});
            skLineSegment(sketch, "E689", {"start": v(3.83, -4.04) * mm, "end": v(3.56, -3.8) * mm});
            skLineSegment(sketch, "E690", {"start": v(3.56, -3.8) * mm, "end": v(3.24, -3.62) * mm});
            skLineSegment(sketch, "E691", {"start": v(3.24, -3.62) * mm, "end": v(2.9, -3.48) * mm});
            skLineSegment(sketch, "E692", {"start": v(2.9, -3.48) * mm, "end": v(2.56, -3.36) * mm});
            skLineSegment(sketch, "E693", {"start": v(2.56, -3.36) * mm, "end": v(2.28, -3.24) * mm});
            skLineSegment(sketch, "E694", {"start": v(2.28, -3.24) * mm, "end": v(2.03, -3.08) * mm});
            skLineSegment(sketch, "E695", {"start": v(2.03, -3.08) * mm, "end": v(1.82, -2.87) * mm});
            skLineSegment(sketch, "E696", {"start": v(1.82, -2.87) * mm, "end": v(1.66, -2.61) * mm});
            skLineSegment(sketch, "E697", {"start": v(1.66, -2.61) * mm, "end": v(1.5, -2.19) * mm});
            skLineSegment(sketch, "E698", {"start": v(1.5, -2.19) * mm, "end": v(1.45, -1.74) * mm});
            skLineSegment(sketch, "E699", {"start": v(1.45, -1.74) * mm, "end": v(1.45, -1.29) * mm});
            skLineSegment(sketch, "E700", {"start": v(1.45, -1.29) * mm, "end": v(1.5, -0.84) * mm});
            skLineSegment(sketch, "E701", {"start": v(1.5, -0.84) * mm, "end": v(1.9, -1.02) * mm});
            skLineSegment(sketch, "E702", {"start": v(1.9, -1.02) * mm, "end": v(2.3, -1.22) * mm});
            skLineSegment(sketch, "E703", {"start": v(2.3, -1.22) * mm, "end": v(2.35, -1.4) * mm});
            skLineSegment(sketch, "E704", {"start": v(2.35, -1.4) * mm, "end": v(2.36, -1.61) * mm});
            skLineSegment(sketch, "E705", {"start": v(2.36, -1.61) * mm, "end": v(2.36, -1.81) * mm});
            skLineSegment(sketch, "E706", {"start": v(2.36, -1.81) * mm, "end": v(2.42, -2) * mm});
            skLineSegment(sketch, "E707", {"start": v(2.42, -2) * mm, "end": v(2.53, -2.2) * mm});
            skLineSegment(sketch, "E708", {"start": v(2.53, -2.2) * mm, "end": v(2.66, -2.36) * mm});
            skLineSegment(sketch, "E709", {"start": v(2.66, -2.36) * mm, "end": v(2.83, -2.5) * mm});
            skLineSegment(sketch, "E710", {"start": v(2.83, -2.5) * mm, "end": v(3.02, -2.59) * mm});
            skLineSegment(sketch, "E711", {"start": v(3.02, -2.59) * mm, "end": v(7.5, -4.13) * mm});
            skLineSegment(sketch, "E712", {"start": v(7.5, -4.13) * mm, "end": v(7.82, -4.17) * mm});
            skLineSegment(sketch, "E713", {"start": v(7.82, -4.17) * mm, "end": v(8.14, -4.11) * mm});
            skLineSegment(sketch, "E714", {"start": v(8.14, -4.11) * mm, "end": v(8.42, -3.95) * mm});
            skLineSegment(sketch, "E715", {"start": v(8.42, -3.95) * mm, "end": v(8.62, -3.7) * mm});
            skLineSegment(sketch, "E716", {"start": v(8.62, -3.7) * mm, "end": v(8.74, -3.24) * mm});
            skLineSegment(sketch, "E717", {"start": v(8.74, -3.24) * mm, "end": v(8.76, -2.78) * mm});
            skLineSegment(sketch, "E718", {"start": v(8.76, -2.78) * mm, "end": v(8.79, -0.1) * mm});
            skLineSegment(sketch, "E719", {"start": v(8.79, -0.1) * mm, "end": v(8.78, 0.46) * mm});
            skLineSegment(sketch, "E720", {"start": v(8.78, 0.46) * mm, "end": v(8.76, 1.02) * mm});
            skLineSegment(sketch, "E721", {"start": v(8.76, 1.02) * mm, "end": v(8.7, 1.24) * mm});
            skLineSegment(sketch, "E722", {"start": v(8.7, 1.24) * mm, "end": v(8.58, 1.43) * mm});
            skLineSegment(sketch, "E723", {"start": v(8.58, 1.43) * mm, "end": v(8.45, 1.6) * mm});
            skLineSegment(sketch, "E724", {"start": v(8.45, 1.6) * mm, "end": v(8.33, 1.8) * mm});
            skLineSegment(sketch, "E725", {"start": v(8.33, 1.8) * mm, "end": v(8.21, 2.07) * mm});
            skLineSegment(sketch, "E726", {"start": v(8.21, 2.07) * mm, "end": v(8.15, 2.36) * mm});
            skLineSegment(sketch, "E727", {"start": v(8.15, 2.36) * mm, "end": v(8.16, 2.66) * mm});
            skLineSegment(sketch, "E728", {"start": v(8.16, 2.66) * mm, "end": v(8.25, 2.94) * mm});
            skLineSegment(sketch, "E729", {"start": v(4.83, 1.6) * mm, "end": v(5.16, 1.82) * mm});
            skLineSegment(sketch, "E730", {"start": v(5.16, 1.82) * mm, "end": v(5.46, 2.09) * mm});
            skLineSegment(sketch, "E731", {"start": v(5.46, 2.09) * mm, "end": v(5.77, 2.36) * mm});
            skLineSegment(sketch, "E732", {"start": v(5.77, 2.36) * mm, "end": v(6.1, 2.57) * mm});
            skLineSegment(sketch, "E733", {"start": v(6.1, 2.57) * mm, "end": v(5.74, 2.18) * mm});
            skLineSegment(sketch, "E734", {"start": v(5.74, 2.18) * mm, "end": v(5.41, 1.74) * mm});
            skLineSegment(sketch, "E735", {"start": v(5.41, 1.74) * mm, "end": v(5.16, 1.27) * mm});
            skLineSegment(sketch, "E736", {"start": v(5.16, 1.27) * mm, "end": v(5, 0.76) * mm});
            skLineSegment(sketch, "E737", {"start": v(5, 0.76) * mm, "end": v(4.96, 0.28) * mm});
            skLineSegment(sketch, "E738", {"start": v(4.96, 0.28) * mm, "end": v(5.02, -0.2) * mm});
            skLineSegment(sketch, "E739", {"start": v(5.02, -0.2) * mm, "end": v(5.18, -0.66) * mm});
            skLineSegment(sketch, "E740", {"start": v(5.18, -0.66) * mm, "end": v(5.4, -1.09) * mm});
            skLineSegment(sketch, "E741", {"start": v(5.4, -1.09) * mm, "end": v(5.22, -1.07) * mm});
            skLineSegment(sketch, "E742", {"start": v(5.22, -1.07) * mm, "end": v(5, -0.7) * mm});
            skLineSegment(sketch, "E743", {"start": v(5, -0.7) * mm, "end": v(4.82, -0.32) * mm});
            skLineSegment(sketch, "E744", {"start": v(4.82, -0.32) * mm, "end": v(4.53, 0.22) * mm});
            skLineSegment(sketch, "E745", {"start": v(4.53, 0.22) * mm, "end": v(4.1, 0.65) * mm});
            skLineSegment(sketch, "E746", {"start": v(4.1, 0.65) * mm, "end": v(3.57, 0.99) * mm});
            skLineSegment(sketch, "E747", {"start": v(3.57, 0.99) * mm, "end": v(2.99, 1.25) * mm});
            skLineSegment(sketch, "E748", {"start": v(2.99, 1.25) * mm, "end": v(2.4, 1.5) * mm});
            skLineSegment(sketch, "E749", {"start": v(2.4, 1.5) * mm, "end": v(1.84, 1.78) * mm});
            skLineSegment(sketch, "E750", {"start": v(1.84, 1.78) * mm, "end": v(1.27, 2.07) * mm});
            skLineSegment(sketch, "E751", {"start": v(1.27, 2.07) * mm, "end": v(0.69, 2.33) * mm});
            skLineSegment(sketch, "E752", {"start": v(0.69, 2.33) * mm, "end": v(0.55, 2.4) * mm});
            skLineSegment(sketch, "E753", {"start": v(0.55, 2.4) * mm, "end": v(0.44, 2.48) * mm});
            skLineSegment(sketch, "E754", {"start": v(0.44, 2.48) * mm, "end": v(0.8, 2.4) * mm});
            skLineSegment(sketch, "E755", {"start": v(0.8, 2.4) * mm, "end": v(2, 1.98) * mm});
            skLineSegment(sketch, "E756", {"start": v(2, 1.98) * mm, "end": v(3.22, 1.61) * mm});
            skLineSegment(sketch, "E757", {"start": v(3.22, 1.61) * mm, "end": v(3.61, 1.5) * mm});
            skLineSegment(sketch, "E758", {"start": v(3.61, 1.5) * mm, "end": v(4.03, 1.43) * mm});
            skLineSegment(sketch, "E759", {"start": v(4.03, 1.43) * mm, "end": v(4.44, 1.46) * mm});
            skLineSegment(sketch, "E760", {"start": v(4.44, 1.46) * mm, "end": v(4.83, 1.6) * mm});
            skSolve(sketch);
        }
        {
            var Q0;
            Q0=makeQuery(id+"F4.imprint","IMPRINT",FACE,{"disambiguationData":[TD([[makeQuery(id+"F4.imprint","IMPRINT",EDGE,{"derivedFrom":sQuery(id+"F4.wireOp",EDGE,"E2")}),-1.0]])]});
            var Q1;
            Q1=makeQuery(id+"F4.imprint","IMPRINT",FACE,{"disambiguationData":[TD([[makeQuery(id+"F4.imprint","IMPRINT",EDGE,{"derivedFrom":sQuery(id+"F4.wireOp",EDGE,"E384")}),-1.0]])]});
            var Q2;
            Q2=makeQuery(id+"F4.imprint","IMPRINT",FACE,{"disambiguationData":[TD([[makeQuery(id+"F4.imprint","IMPRINT",EDGE,{"derivedFrom":sQuery(id+"F4.wireOp",EDGE,"E519")}),-1.0]])]});
            var Q3;
            Q3=makeQuery(id+"F4.imprint","IMPRINT",FACE,{"disambiguationData":[TD([[makeQuery(id+"F4.imprint","IMPRINT",EDGE,{"derivedFrom":sQuery(id+"F4.wireOp",EDGE,"E556")}),-1.0]])]});
            var Q4;
            Q4=makeQuery(id+"F4.imprint","IMPRINT",FACE,{"disambiguationData":[TD([[makeQuery(id+"F4.imprint","IMPRINT",EDGE,{"derivedFrom":sQuery(id+"F4.wireOp",EDGE,"E500")}),-1.0]])]});
            var Q5;
            Q5=makeQuery(id+"F4.imprint","IMPRINT",FACE,{"disambiguationData":[TD([[makeQuery(id+"F4.imprint","IMPRINT",EDGE,{"derivedFrom":sQuery(id+"F4.wireOp",EDGE,"E479")}),-1.0]])]});
            var Q6;
            Q6=makeQuery(id+"F4.imprint","IMPRINT",FACE,{"disambiguationData":[TD([[makeQuery(id+"F4.imprint","IMPRINT",EDGE,{"derivedFrom":sQuery(id+"F4.wireOp",EDGE,"E464")}),-1.0]])]});
            var Q7;
            Q7=makeQuery(id+"F4.imprint","IMPRINT",FACE,{"disambiguationData":[TD([[makeQuery(id+"F4.imprint","IMPRINT",EDGE,{"derivedFrom":sQuery(id+"F4.wireOp",EDGE,"E443")}),-1.0]])]});
            var Q8;
            Q8=makeQuery(id+"F4.imprint","IMPRINT",FACE,{"disambiguationData":[TD([[makeQuery(id+"F4.imprint","IMPRINT",EDGE,{"derivedFrom":sQuery(id+"F4.wireOp",EDGE,"E424")}),-1.0]])]});
            var Q9;
            Q9=makeQuery(id+"F4.imprint","IMPRINT",FACE,{"disambiguationData":[TD([[makeQuery(id+"F4.imprint","IMPRINT",EDGE,{"derivedFrom":sQuery(id+"F4.wireOp",EDGE,"E400")}),-1.0]])]});
            extrude(context, id + "F5", {"entities" : qUnion([Q0, Q1, Q2, Q3, Q4, Q5, Q6, Q7, Q8, Q9]), "operationType" : NewBodyOperationType.REMOVE, "oppositeDirection" : true, "depth" : 2 * mm});
        }
    });
